FCSTD DOCUMENT  (FreeCAD 1.0R39285 (Git))
Label: full_assembly
License: All rights reserved
LicenseURL: http://en.wikipedia.org/wiki/All_rights_reserved
objects: App::Link×6, App::FeaturePython×6, Assembly::JointGroup×1, Assembly::AssemblyObject×1
EXTERNAL_REF file=front_plate.FCStd obj=Body
EXTERNAL_REF file=bottom_plate.FCStd obj=Body
EXTERNAL_REF file=side_left.FCStd obj=Clone
EXTERNAL_REF file=side_right.FCStd obj=Body
EXTERNAL_REF file=button.FCStd obj=Body
EXTERNAL_REF file=obd_wire_top.FCStd obj=Body

FEATURE [App::Link] Body
  LinkedObject = -> <external front_plate.FCStd>#Body
FEATURE [App::FeaturePython] GroundedJoint  # Assembly grounded joint (typed FeaturePython)
  ObjectToGround = -> Body
FEATURE [App::Link] Body001
  LinkPlacement = pos=(-1.29e-14,-21.3868,-88.9) rot=(1,0,0;4.71239rad)
  LinkedObject = -> <external bottom_plate.FCStd>#Body
  Placement = pos=(-1.29e-14,-21.3868,-88.9) rot=(1,0,0;4.71239rad)
FEATURE [App::Link] Hole001
  LinkPlacement = pos=(-84.328,1e-16,-76.2) rot=(0,-1,0;1.5708rad)
  LinkedObject = -> <external side_left.FCStd>#Clone
  Placement = pos=(-84.328,1e-16,-76.2) rot=(0,-1,0;1.5708rad)
FEATURE [App::Link] Body002
  LinkPlacement = pos=(84.328,-1.07e-14,-76.2) rot=(0,1,0;4.71239rad)
  LinkedObject = -> <external side_right.FCStd>#Body
  Placement = pos=(84.328,-1.07e-14,-76.2) rot=(0,1,0;4.71239rad)
FEATURE [App::FeaturePython] Joint  label="Fixed"  # Assembly joint (typed FeaturePython)
  Activated = true
  AngleMax = 0
  AngleMin = 0
  Detach1 = false
  Detach2 = false
  Distance = 0
  Distance2 = 0
  EnableAngleMax = false
  EnableAngleMin = false
  EnableLengthMax = false
  EnableLengthMin = false
  JointType = 0 (Fixed)
  LengthMax = 0
  LengthMin = 0
  Placement1 = pos=(-84.328,12.7,-19.05) rot=(0.707107,0,0.707107;3.14159rad)
  Placement2 = pos=(57.15,12.7,0) rot=(0,0,1;0rad)
  Reference1 = -> Assembly [Body.Edge87,Body.Edge87]
  Reference2 = -> Assembly [Hole001.Edge12,Hole001.Edge12]
FEATURE [App::FeaturePython] Joint002  label="Fixed002"  # Assembly joint (typed FeaturePython)
  Activated = true
  AngleMax = 0
  AngleMin = 0
  Detach1 = false
  Detach2 = false
  Distance = 0
  Distance2 = 0
  EnableAngleMax = false
  EnableAngleMin = false
  EnableLengthMax = false
  EnableLengthMin = false
  JointType = 0 (Fixed)
  LengthMax = 0
  LengthMin = 0
  Offset2 = pos=(0,0,0) rot=(0,0,-1;1.5708rad)
  Placement1 = pos=(74.168,-45.72,0) rot=(0,0,1;0rad)
  Placement2 = pos=(33.02,-21.3868,10.16) rot=(0.57735,-0.57735,-0.57735;4.18879rad)
  Reference1 = -> Assembly [Body001.?Edge13,Body001.?Edge13]
  Reference2 = -> Assembly [Body002.Edge68,Body002.Edge68]
FEATURE [App::Link] Body003
  LinkPlacement = pos=(43.2139,20.4026,-0.30034) rot=(0,0,1;0rad)
  LinkedObject = -> <external button.FCStd>#Body
  Placement = pos=(43.2139,20.4026,-0.30034) rot=(0,0,1;0rad)
FEATURE [App::FeaturePython] Joint003  label="Slider"  # Assembly joint (typed FeaturePython)
  Activated = true
  AngleMax = 0
  AngleMin = 0
  Detach1 = false
  Detach2 = false
  Distance = 0
  Distance2 = 0
  EnableAngleMax = false
  EnableAngleMin = false
  EnableLengthMax = false
  EnableLengthMin = false
  JointType = 3 (Slider)
  LengthMax = 0
  LengthMin = 0
  Placement1 = pos=(43.2139,20.4026,4.0132) rot=(0,0,1;0rad)
  Placement2 = pos=(0,0,5.08) rot=(0,0,1;0rad)
  Reference1 = -> Assembly [Body.Edge71,Body.Edge71]
  Reference2 = -> Assembly [Body003.Face4,Body003.Face4]
FEATURE [App::FeaturePython] Joint004  label="Fixed003"  # Assembly joint (typed FeaturePython)
  Activated = true
  AngleMax = 0
  AngleMin = 0
  Detach1 = false
  Detach2 = false
  Distance = 0
  Distance2 = 0
  EnableAngleMax = false
  EnableAngleMin = false
  EnableLengthMax = false
  EnableLengthMin = false
  JointType = 0 (Fixed)
  LengthMax = 0
  LengthMin = 0
  Placement1 = pos=(84.328,12.7,-19.05) rot=(0,-1,0;1.5708rad)
  Placement2 = pos=(57.15,12.7,0) rot=(0,0,1;0rad)
  Reference1 = -> Assembly [Body.Face48,Body.Edge1]
  Reference2 = -> Assembly [Body002.Face13,Body002.Edge3]
FEATURE [App::Link] Body004
  LinkPlacement = pos=(3.77944,9.05724,-256.163) rot=(0.57735,0.57735,-0.57735;2.0944rad)
  LinkedObject = -> <external obd_wire_top.FCStd>#Body
  Placement = pos=(3.77944,9.05724,-256.163) rot=(0.57735,0.57735,-0.57735;2.0944rad)
FEATURE [App::FeaturePython] GroundedJoint001  # Assembly grounded joint (typed FeaturePython)
  ObjectToGround = -> Body001
  Placement = pos=(-1.29e-14,-21.3868,-88.9) rot=(1,0,0;4.71239rad)
FEATURE [Assembly::JointGroup] Joints
  Group = -> [GroundedJoint,Joint,Joint002,Joint003,Joint004,GroundedJoint001]
FEATURE [Assembly::AssemblyObject] Assembly
  Group = -> [Joints,Body,GroundedJoint,Body001,Hole001,Body002,Joint,Joint002,Body003,Joint003,Joint004,GroundedJoint001,Body004]
  Origin = -> Origin
  Type = Assembly

RESOLVED EXTERNAL PARTS (link-assembly join: the EXTERNAL_REF files above that resolve inside this repo's crawl, each included once):
---- part bottom_plate.FCStd = doc fcstd_007f6532ab22 ----
FCSTD DOCUMENT  (FreeCAD 1.0R39285 (Git))
Label: bottom_plate
License: All rights reserved
LicenseURL: http://en.wikipedia.org/wiki/All_rights_reserved
objects: PartDesign::Pad×7, Sketcher::SketchObject×5, PartDesign::Plane×4, PartDesign::Pocket×1, PartDesign::Fillet×1, PartDesign::Body×1, Measure::MeasureLength×1
note: 42 computed .brp shape members not serialized (recipe doc carries the construction recipe); baked Part::Feature solids carry a one-line shape summary decoded from their .brp

FEATURE [Sketcher::SketchObject] Sketch
  ArcFitTolerance = 1e-06
  AttachmentSupport = -> [XY_Plane]
  FullyConstrained = true
  MakeInternals = false
  MapMode = 5
  sketch-geometry (13):
    g0: LineSegment StartX=-79.248 StartY=50.8 StartZ=0 EndX=-79.248 EndY=-50.8 EndZ=0
    g1: LineSegment StartX=-79.248 StartY=-50.8 StartZ=0 EndX=79.248 EndY=-50.8 EndZ=0
    g2: LineSegment StartX=79.248 StartY=-50.8 StartZ=0 EndX=79.248 EndY=50.8 EndZ=0
    g3: LineSegment StartX=79.248 StartY=50.8 StartZ=0 EndX=-79.248 EndY=50.8 EndZ=0
    g4: GeomPoint [constr] X=0 Y=0 Z=0
    g5: LineSegment [constr] StartX=-79.248 StartY=50.8 StartZ=0 EndX=-74.168 EndY=45.72 EndZ=0
    g6: LineSegment [constr] StartX=-79.248 StartY=-50.8 StartZ=0 EndX=-74.168 EndY=-45.72 EndZ=0
    g7: LineSegment [constr] StartX=79.248 StartY=-50.8 StartZ=0 EndX=74.168 EndY=-45.72 EndZ=0
    g8: LineSegment [constr] StartX=79.248 StartY=50.8 StartZ=0 EndX=74.168 EndY=45.72 EndZ=0
    g9: Circle CenterX=-74.168 CenterY=45.72 CenterZ=0 NormalX=0 NormalY=0 NormalZ=1 AngleXU=0 Radius=1.5875
    g10: Circle CenterX=-74.168 CenterY=-45.72 CenterZ=0 NormalX=0 NormalY=0 NormalZ=1 AngleXU=0 Radius=1.5875
    g11: Circle CenterX=74.168 CenterY=-45.72 CenterZ=0 NormalX=0 NormalY=0 NormalZ=1 AngleXU=0 Radius=1.5875
    g12: Circle CenterX=74.168 CenterY=45.72 CenterZ=0 NormalX=0 NormalY=0 NormalZ=1 AngleXU=0 Radius=1.5875
  constraints (32):
    c: Coincident(g0,g1)
    c: Coincident(g1,g2)
    c: Coincident(g2,g3)
    c: Coincident(g3,g0)
    c: Vertical(g0)
    c: Vertical(g2)
    c: Horizontal(g1)
    c: Horizontal(g3)
    c: Symmetric(g2,g0,g4)
    c: Distance(g0,g2) = 158.496
    c: Coincident(g4,g-1)
    c: Distance(g0,g0) = 101.6
    c: DistanceX(g5,g5) = 5.08
    c: DistanceY(g5,g5) = 5.08
    c: Coincident(g5,g0)
    c: DistanceX(g6,g6) = 5.08
    c: DistanceY(g6,g6) = 5.08
    c: Coincident(g6,g0)
    c: DistanceX(g7,g7) = 5.08
    c: DistanceY(g7,g7) = 5.08
    c: Coincident(g7,g1)
    c: DistanceX(g8,g8) = 5.08
    c: DistanceY(g8,g8) = 5.08
    c: Coincident(g8,g2)
    c: Diameter(g9) = 3.175
    c: Coincident(g9,g5)
    c: Diameter(g10) = 3.175
    c: Coincident(g10,g6)
    c: Diameter(g11) = 3.175
    c: Coincident(g11,g7)
    c: Diameter(g12) = 3.175
    c: Coincident(g12,g8)
FEATURE [PartDesign::Pad] Pad
  Direction = (0,0,1)
  Length = 4.0132
  Length2 = 10
  Profile = -> Sketch
  ReferenceAxis = -> Sketch [N_Axis]
  Suppressed = false
  Type = 0
FEATURE [PartDesign::Pad] Pad001
  BaseFeature = -> Pad
  Direction = (0,-1,0)
  Length = 25.4
  Length2 = 10
  Profile = -> Pad [Face2]
  Refine = true
  Suppressed = false
  Type = 0
FEATURE [PartDesign::Plane] DatumPlane
  AttachmentSupport = -> [Pad001]
  Length = 186.871
  MapMode = 5
  Placement = pos=(0,0,4.0132) rot=(0,0,1;0rad)
  ResizeMode = 0
  Width = 155.375
FEATURE [Sketcher::SketchObject] Sketch001
  ArcFitTolerance = 1e-06
  AttachmentSupport = -> [Pad001]
  ExternalGeometry = -> [Pad001]
  FullyConstrained = false
  MakeInternals = false
  MapMode = 5
  Placement = pos=(0,0,4.0132) rot=(0,0,1;0rad)
  sketch-geometry (59):
    g0: LineSegment [constr] StartX=14.4313 StartY=-24.9319 StartZ=0 EndX=14.4313 EndY=-63.0319 EndZ=0
    g1: LineSegment [constr] StartX=14.4313 StartY=-63.0319 StartZ=0 EndX=65.2313 EndY=-63.0319 EndZ=0
    g2: LineSegment [constr] StartX=65.2313 StartY=-63.0319 StartZ=0 EndX=65.2313 EndY=-24.9319 EndZ=0
    g3: LineSegment [constr] StartX=65.2313 StartY=-24.9319 StartZ=0 EndX=14.4313 EndY=-24.9319 EndZ=0
    g4: LineSegment [constr] StartX=-65.2313 StartY=-24.9319 StartZ=0 EndX=-65.2313 EndY=-63.0319 EndZ=0
    g5: LineSegment [constr] StartX=-65.2313 StartY=-63.0319 StartZ=0 EndX=-14.4313 EndY=-63.0319 EndZ=0
    g6: LineSegment [constr] StartX=-14.4313 StartY=-63.0319 StartZ=0 EndX=-14.4313 EndY=-24.9319 EndZ=0
    g7: LineSegment [constr] StartX=-14.4313 StartY=-24.9319 StartZ=0 EndX=-65.2313 EndY=-24.9319 EndZ=0
    g8: LineSegment [constr] StartX=-14.4313 StartY=-63.0319 StartZ=0 EndX=14.4313 EndY=-63.0319 EndZ=0
    g9: LineSegment [constr] StartX=-65.2313 StartY=43.3911 StartZ=0 EndX=-65.2313 EndY=-8.67892 EndZ=0
    g10: LineSegment [constr] StartX=-65.2313 StartY=-8.67892 StartZ=0 EndX=23.6687 EndY=-8.67892 EndZ=0
    g11: LineSegment [constr] StartX=23.6687 StartY=-8.67892 StartZ=0 EndX=23.6687 EndY=43.3911 EndZ=0
    g12: LineSegment [constr] StartX=23.6687 StartY=43.3911 StartZ=0 EndX=-65.2313 EndY=43.3911 EndZ=0
    g13: LineSegment [constr] StartX=45.5463 StartY=-8.67892 StartZ=0 EndX=65.2313 EndY=-8.67892 EndZ=0
    g14: LineSegment [constr] StartX=65.2313 StartY=-8.67892 StartZ=0 EndX=65.2313 EndY=37.4221 EndZ=0
    g15: LineSegment [constr] StartX=65.2313 StartY=37.4221 StartZ=0 EndX=45.5463 EndY=37.4221 EndZ=0
    g16: LineSegment [constr] StartX=45.5463 StartY=37.4221 StartZ=0 EndX=45.5463 EndY=-8.67892 EndZ=0
    g17: LineSegment [constr] StartX=-65.2313 StartY=-63.0319 StartZ=0 EndX=-79.248 EndY=-63.0319 EndZ=0
    g18: LineSegment [constr] StartX=65.2313 StartY=-63.0319 StartZ=0 EndX=79.248 EndY=-63.0319 EndZ=0
    g19: LineSegment [constr] StartX=-65.2313 StartY=-8.67892 StartZ=0 EndX=65.2313 EndY=-8.67892 EndZ=0
    g20: LineSegment [constr] StartX=19.5748 StartY=-43.9819 StartZ=0 EndX=60.0878 EndY=-43.9819 EndZ=0
    g21: LineSegment [constr] StartX=60.0878 StartY=-43.9819 StartZ=0 EndX=60.0878 EndY=-63.0319 EndZ=0
    g22: LineSegment [constr] StartX=60.0878 StartY=-43.9819 StartZ=0 EndX=60.0878 EndY=-24.9319 EndZ=0
    g23: LineSegment [constr] StartX=60.0878 StartY=-43.9819 StartZ=0 EndX=65.2313 EndY=-43.9819 EndZ=0
    g24: LineSegment [constr] StartX=19.5748 StartY=-43.9819 StartZ=0 EndX=14.4313 EndY=-43.9819 EndZ=0
    g25: LineSegment [constr] StartX=-65.2313 StartY=-43.9819 StartZ=0 EndX=-60.0878 EndY=-43.9819 EndZ=0
    g26: LineSegment [constr] StartX=-14.4313 StartY=-43.9819 StartZ=0 EndX=-19.5748 EndY=-43.9819 EndZ=0
    g27: LineSegment [constr] StartX=-60.0878 StartY=-43.9819 StartZ=0 EndX=-19.5748 EndY=-43.9819 EndZ=0
    g28: LineSegment [constr] StartX=-65.2313 StartY=17.3561 StartZ=0 EndX=-57.6113 EndY=17.3561 EndZ=0
    g29: LineSegment [constr] StartX=23.6687 StartY=17.3561 StartZ=0 EndX=16.0487 EndY=17.3561 EndZ=0
    g30: LineSegment [constr] StartX=-57.6113 StartY=17.3561 StartZ=0 EndX=16.0487 EndY=17.3561 EndZ=0
    g31: LineSegment [constr] StartX=55.3888 StartY=-8.67892 StartZ=0 EndX=55.3888 EndY=7.06908 EndZ=0
    g32: LineSegment [constr] StartX=55.3888 StartY=37.4221 StartZ=0 EndX=55.3888 EndY=21.6741 EndZ=0
    g33: LineSegment [constr] StartX=55.3888 StartY=7.06908 StartZ=0 EndX=55.3888 EndY=21.6741 EndZ=0
    g34: Circle CenterX=-60.0878 CenterY=-43.9819 CenterZ=0 NormalX=0 NormalY=0 NormalZ=1 AngleXU=0 Radius=2.54
    g35: Circle CenterX=-19.5748 CenterY=-43.9819 CenterZ=0 NormalX=0 NormalY=0 NormalZ=1 AngleXU=0 Radius=2.54
    g36: Circle CenterX=19.5748 CenterY=-43.9819 CenterZ=0 NormalX=0 NormalY=0 NormalZ=1 AngleXU=0 Radius=2.54
    g37: Circle CenterX=60.0878 CenterY=-43.9819 CenterZ=0 NormalX=0 NormalY=0 NormalZ=1 AngleXU=0 Radius=2.54
    g38: Circle CenterX=16.0487 CenterY=17.3561 CenterZ=0 NormalX=0 NormalY=0 NormalZ=1 AngleXU=0 Radius=2.54
    g39: Circle CenterX=55.3888 CenterY=7.06908 CenterZ=0 NormalX=0 NormalY=0 NormalZ=1 AngleXU=0 Radius=2.54
    g40: Circle CenterX=55.3888 CenterY=21.6741 CenterZ=0 NormalX=0 NormalY=0 NormalZ=1 AngleXU=0 Radius=2.54
    g41: Circle CenterX=-57.6113 CenterY=17.3561 CenterZ=0 NormalX=0 NormalY=0 NormalZ=1 AngleXU=0 Radius=2.54
    g42: LineSegment [constr] StartX=65.2313 StartY=-24.9319 StartZ=0 EndX=65.2313 EndY=-8.67892 EndZ=0
    g43: LineSegment [constr] StartX=-65.2313 StartY=-8.67892 StartZ=0 EndX=-65.2313 EndY=-24.9319 EndZ=0
    g44: Circle CenterX=-57.6113 CenterY=17.3561 CenterZ=0 NormalX=0 NormalY=0 NormalZ=1 AngleXU=0 Radius=0.992188
    g45: Circle CenterX=-19.5748 CenterY=-43.9819 CenterZ=0 NormalX=0 NormalY=0 NormalZ=1 AngleXU=0 Radius=0.992188
    g46: Circle CenterX=19.5748 CenterY=-43.9819 CenterZ=0 NormalX=0 NormalY=0 NormalZ=1 AngleXU=0 Radius=0.992188
    g47: Circle CenterX=55.3888 CenterY=7.06908 CenterZ=0 NormalX=0 NormalY=0 NormalZ=1 AngleXU=0 Radius=0.992188
    g48: Circle CenterX=55.3888 CenterY=21.6741 CenterZ=0 NormalX=0 NormalY=0 NormalZ=1 AngleXU=0 Radius=0.992188
    g49: LineSegment [constr] StartX=-65.2313 StartY=-16.8054 StartZ=0 EndX=-79.248 EndY=-16.8054 EndZ=0
    g50: LineSegment StartX=-74.1447 StartY=-24.1079 StartZ=0 EndX=-70.3347 EndY=-24.1079 EndZ=0
    g51: LineSegment StartX=-70.3347 StartY=-24.1079 StartZ=0 EndX=-70.3347 EndY=-9.5029 EndZ=0
    g52: LineSegment StartX=-70.3347 StartY=-9.5029 StartZ=0 EndX=-74.1447 EndY=-9.5029 EndZ=0
    g53: LineSegment StartX=-74.1447 StartY=-9.5029 StartZ=0 EndX=-74.1447 EndY=-24.1079 EndZ=0
    g54: GeomPoint [constr] X=-72.2397 Y=-16.8054 Z=0
    g55: LineSegment [constr] StartX=-72.2397 StartY=-24.1079 StartZ=0 EndX=-72.2397 EndY=-22.2029 EndZ=0
    g56: LineSegment [constr] StartX=-72.2397 StartY=-9.5029 StartZ=0 EndX=-72.2397 EndY=-11.4079 EndZ=0
    g57: Circle CenterX=-72.2397 CenterY=-11.4079 CenterZ=0 NormalX=0 NormalY=0 NormalZ=1 AngleXU=0 Radius=0.992188
    g58: Circle CenterX=-72.2397 CenterY=-22.2029 CenterZ=0 NormalX=0 NormalY=0 NormalZ=1 AngleXU=0 Radius=0.992188
  constraints (148):
    c: Coincident(g0,g1)
    c: Coincident(g1,g2)
    c: Coincident(g2,g3)
    c: Coincident(g3,g0)
    c: Vertical(g0)
    c: Vertical(g2)
    c: Horizontal(g1)
    c: Horizontal(g3)
    c: Coincident(g4,g5)
    c: Coincident(g5,g6)
    c: Coincident(g6,g7)
    c: Coincident(g7,g4)
    c: Vertical(g4)
    c: Vertical(g6)
    c: Horizontal(g5)
    c: Horizontal(g7)
    c: Distance(g4,g6) = 50.8
    c: Distance(g5,g7) = 38.1
    c: Coincident(g8,g5)
    c: Coincident(g8,g0)
    c: Horizontal(g8)
    c: Coincident(g9,g10)
    c: Coincident(g10,g11)
    c: Coincident(g11,g12)
    c: Coincident(g12,g9)
    c: Vertical(g9)
    c: Vertical(g11)
    c: Horizontal(g10)
    c: Horizontal(g12)
    c: Distance(g9,g11) = 88.9
    c: Distance(g10,g12) = 52.07
    c: Coincident(g13,g14)
    c: Coincident(g14,g15)
    c: Coincident(g15,g16)
    c: Coincident(g16,g13)
    c: Horizontal(g13)
    c: Horizontal(g15)
    c: Vertical(g14)
    c: Vertical(g16)
    c: Distance(g14,g16) = 19.685
    c: Distance(g13,g15) = 46.101
    c: Coincident(g17,g4)
    c: PointOnObject(g17,g-4)
    c: Horizontal(g17)
    c: Coincident(g18,g1)
    c: PointOnObject(g18,g-6)
    c: Horizontal(g18)
    c: Equal(g18,g17)
    c: Coincident(g19,g9)
    c: Coincident(g19,g13)
    c: Horizontal(g19)
    c: Distance(g20) = 40.513
    c: Horizontal(g20)
    c: Coincident(g21,g20)
    c: PointOnObject(g21,g1)
    c: Vertical(g21)
    c: Coincident(g22,g20)
    c: PointOnObject(g22,g3)
    c: Vertical(g22)
    c: Coincident(g23,g20)
    c: Symmetric(g2,g2,g23)
    c: Coincident(g24,g20)
    c: Symmetric(g0,g0,g24)
    c: Equal(g22,g21)
    c: Equal(g23,g24)
    c: Symmetric(g4,g4,g25)
    c: Horizontal(g25)
    c: Symmetric(g6,g6,g26)
    c: Horizontal(g26)
    c: Coincident(g27,g25)
    c: Coincident(g27,g26)
    c: DistanceX(g27,g27) = 40.513
    c: Equal(g26,g25)
    c: Symmetric(g9,g9,g28)
    c: Horizontal(g28)
    c: Symmetric(g11,g11,g29)
    c: Horizontal(g29)
    c: Coincident(g30,g28)
    c: Coincident(g30,g29)
    c: DistanceX(g30,g30) = 73.66
    c: Equal(g29,g28)
    c: Symmetric(g13,g13,g31)
    c: Vertical(g31)
    c: Symmetric(g15,g15,g32)
    c: Vertical(g32)
    c: Coincident(g33,g31)
    c: Coincident(g33,g32)
    c: DistanceY(g33,g33) = 14.605
    c: Equal(g32,g31)
    c: Diameter(g34) = 5.08
    c: Coincident(g34,g25)
    c: Diameter(g35) = 5.08
    c: Coincident(g35,g26)
    c: Diameter(g36) = 5.08
    c: Coincident(g36,g20)
    c: Diameter(g37) = 5.08
    c: Coincident(g37,g20)
    c: Diameter(g38) = 5.08
    c: Coincident(g38,g29)
    c: Diameter(g39) = 5.08
    c: Coincident(g39,g31)
    c: Diameter(g40) = 5.08
    c: Coincident(g40,g32)
    c: Equal(g7,g3)
    c: Equal(g4,g0)
    c: Diameter(g41) = 5.08
    c: Coincident(g41,g28)
    c: Coincident(g42,g2)
    c: Coincident(g42,g13)
    c: Coincident(g43,g9)
    c: Coincident(g43,g4)
    c: Vertical(g43)
    c: Vertical(g42)
    c: Diameter(g44) = 1.98438
    c: Coincident(g44,g28)
    c: Coincident(g45,g26)
    c: Coincident(g46,g20)
    c: Coincident(g47,g31)
    c: Coincident(g48,g32)
    c: Equal(g44,g45)
    c: Equal(g46,g44)
    c: Equal(g44,g47)
    c: Equal(g47,g48)
    c: Symmetric(g43,g43,g49)
    c: PointOnObject(g49,g-4)
    c: Horizontal(g49)
    c: Coincident(g50,g51)
    c: Coincident(g51,g52)
    c: Coincident(g52,g53)
    c: Coincident(g53,g50)
    c: Horizontal(g50)
    c: Horizontal(g52)
    c: Vertical(g51)
    c: Vertical(g53)
    c: Symmetric(g52,g50,g54)
    c: Distance(g51,g53) = 3.81
    c: Distance(g50,g52) = 14.605
    c: Symmetric(g49,g49,g54)
    c: Distance(g55) = 1.905
    c: Symmetric(g50,g50,g55)
    c: Vertical(g55)
    c: Distance(g56) = 1.905
    c: Symmetric(g52,g52,g56)
    c: Vertical(g56)
    c: Diameter(g57) = 1.98438
    c: Coincident(g57,g56)
    c: Coincident(g58,g55)
    c: Equal(g57,g58)
FEATURE [PartDesign::Pad] Pad002
  BaseFeature = -> Pad001
  Direction = (0,0,1)
  Length = 7.62
  Length2 = 10
  Profile = -> Sketch001
  ReferenceAxis = -> Sketch001 [N_Axis]
  Refine = true
  Suppressed = false
  Type = 0
FEATURE [PartDesign::Pad] Pad003
  BaseFeature = -> Pad002
  Direction = (0,0,1)
  Length = 0.254
  Length2 = 10
  Profile = -> Pad002 [Face23,Face27]
  Refine = true
  Suppressed = false
  Type = 0
FEATURE [PartDesign::Pad] Pad004
  BaseFeature = -> Pad003
  Direction = (0,0,1)
  Length = 0.508
  Length2 = 10
  Profile = -> Pad003 [Face25]
  Refine = true
  Suppressed = false
  Type = 0
FEATURE [PartDesign::Plane] DatumPlane001
  AttachmentSupport = -> [Pad004]
  Length = 186.871
  MapMode = 5
  Placement = pos=(0,0,11.8872) rot=(0,0,1;0rad)
  ResizeMode = 0
  Width = 155.375
FEATURE [Sketcher::SketchObject] Sketch002
  ArcFitTolerance = 1e-06
  AttachmentSupport = -> [Pad004]
  ExternalGeometry = -> [Pad004]
  FullyConstrained = true
  MakeInternals = false
  MapMode = 5
  Placement = pos=(0,0,11.8872) rot=(0,0,1;0rad)
  sketch-geometry (2):
    g0: Circle CenterX=60.0878 CenterY=-43.9819 CenterZ=0 NormalX=0 NormalY=0 NormalZ=1 AngleXU=0 Radius=1.4605
    g1: Circle CenterX=-60.0878 CenterY=-43.9819 CenterZ=0 NormalX=0 NormalY=0 NormalZ=1 AngleXU=0 Radius=1.4605
  constraints (4):
    c: Diameter(g0) = 2.921
    c: Coincident(g0,g-4)
    c: Diameter(g1) = 2.921
    c: Coincident(g1,g-3)
FEATURE [PartDesign::Pad] Pad005
  BaseFeature = -> Pad004
  Direction = (0,0,1)
  Length = 1.524
  Length2 = 10
  Profile = -> Sketch002
  ReferenceAxis = -> Sketch002 [N_Axis]
  Refine = true
  Suppressed = false
  Type = 0
FEATURE [PartDesign::Plane] DatumPlane002
  AttachmentSupport = -> [Pad005]
  Length = 155.375
  MapMode = 11
  Placement = pos=(16.0487,17.3561,12.1412) rot=(0,0,1;1.5708rad)
  ResizeMode = 0
  Width = 186.871
FEATURE [Sketcher::SketchObject] Sketch003
  ArcFitTolerance = 1e-06
  AttachmentSupport = -> [DatumPlane002]
  ExternalGeometry = -> [Pad005]
  FullyConstrained = true
  MakeInternals = false
  MapMode = 5
  Placement = pos=(16.0487,17.3561,12.1412) rot=(0,0,1;1.5708rad)
  sketch-geometry (1):
    g0: Circle CenterX=0 CenterY=0 CenterZ=0 NormalX=0 NormalY=0 NormalZ=1 AngleXU=0 Radius=1.4605
  constraints (2):
    c: Diameter(g0) = 2.921
    c: Coincident(g0,g-1)
FEATURE [PartDesign::Pad] Pad006
  BaseFeature = -> Pad005
  Direction = (0,0,1)
  Length = 1.524
  Length2 = 10
  Profile = -> Sketch003
  ReferenceAxis = -> Sketch003 [N_Axis]
  Refine = true
  Suppressed = false
  Type = 0
FEATURE [PartDesign::Plane] DatumPlane003
  AttachmentSupport = -> [Pad003]
  Length = 142.937
  MapMode = 5
  Placement = pos=(-74.1447,0,0) rot=(0.57735,-0.57735,-0.57735;2.0944rad)
  ResizeMode = 0
  Width = 65.9374
FEATURE [Sketcher::SketchObject] Sketch004
  ArcFitTolerance = 1e-06
  AttachmentSupport = -> [Pad003]
  ExternalGeometry = -> [Pad003]
  FullyConstrained = true
  MakeInternals = false
  MapMode = 5
  Placement = pos=(-74.1447,0,0) rot=(0.57735,-0.57735,-0.57735;2.0944rad)
  sketch-geometry (1):
    g0: Circle CenterX=16.8054 CenterY=11.6332 CenterZ=0 NormalX=0 NormalY=0 NormalZ=1 AngleXU=0 Radius=3.4925
  constraints (2):
    c: Diameter(g0) = 6.985
    c: Symmetric(g-3,g-3,g0)
FEATURE [PartDesign::Pocket] Pocket
  BaseFeature = -> Pad006
  Direction = (1,0,0)
  Length = 5
  Length2 = 5
  Profile = -> Sketch004
  ReferenceAxis = -> Sketch004 [N_Axis]
  Refine = true
  Suppressed = false
  Type = 1
FEATURE [PartDesign::Fillet] Fillet
  Base = -> Pocket [Edge18,Edge19,Edge29,Edge27,Edge24,Edge31,Edge30,Edge25]
  BaseFeature = -> Pocket
  Radius = 3.175
  Refine = true
  SupportTransform = false
  Suppressed = false
  UseAllEdges = false
FEATURE [PartDesign::Body] Body
  AllowCompound = false
  Group = -> [Sketch,Pad,Pad001,DatumPlane,Sketch001,Pad002,Pad003,Pad004,DatumPlane001,Sketch002,Pad005,DatumPlane002,Sketch003,Pad006,DatumPlane003,Sketch004,Pocket,Fillet]
  Origin = -> Origin
  Tip = -> Fillet
FEATURE [Measure::MeasureLength] Length  label="Length: 0.1580 ""
  Elements = -> [Body]
  Length = 4.0132
---- part button.FCStd = doc fcstd_32a29ad11dd7 ----
FCSTD DOCUMENT  (FreeCAD 1.0R39285 (Git))
Label: button
License: All rights reserved
LicenseURL: http://en.wikipedia.org/wiki/All_rights_reserved
objects: PartDesign::Pad×3, Sketcher::SketchObject×2, PartDesign::Pocket×2, PartDesign::Fillet×1, PartDesign::Body×1
note: 23 computed .brp shape members not serialized (recipe doc carries the construction recipe); baked Part::Feature solids carry a one-line shape summary decoded from their .brp

FEATURE [Sketcher::SketchObject] Sketch
  ArcFitTolerance = 1e-06
  AttachmentSupport = -> [XY_Plane]
  FullyConstrained = true
  MakeInternals = false
  MapMode = 5
  sketch-geometry (10):
    g0: LineSegment StartX=-1.6129 StartY=-1.1049 StartZ=0 EndX=1.6129 EndY=-1.1049 EndZ=0
    g1: LineSegment StartX=1.6129 StartY=-1.1049 StartZ=0 EndX=1.6129 EndY=1.1049 EndZ=0
    g2: LineSegment StartX=1.6129 StartY=1.1049 StartZ=0 EndX=-1.6129 EndY=1.1049 EndZ=0
    g3: LineSegment StartX=-1.6129 StartY=1.1049 StartZ=0 EndX=-1.6129 EndY=-1.1049 EndZ=0
    g4: GeomPoint [constr] X=0 Y=0 Z=0
    g5: LineSegment StartX=-1.905 StartY=-1.905 StartZ=0 EndX=1.905 EndY=-1.905 EndZ=0
    g6: LineSegment StartX=1.905 StartY=-1.905 StartZ=0 EndX=1.905 EndY=1.905 EndZ=0
    g7: LineSegment StartX=1.905 StartY=1.905 StartZ=0 EndX=-1.905 EndY=1.905 EndZ=0
    g8: LineSegment StartX=-1.905 StartY=1.905 StartZ=0 EndX=-1.905 EndY=-1.905 EndZ=0
    g9: GeomPoint [constr] X=0 Y=0 Z=0
  constraints (24):
    c: Coincident(g0,g1)
    c: Coincident(g1,g2)
    c: Coincident(g2,g3)
    c: Coincident(g3,g0)
    c: Horizontal(g0)
    c: Horizontal(g2)
    c: Vertical(g1)
    c: Vertical(g3)
    c: Symmetric(g2,g0,g4)
    c: Distance(g1,g3) = 3.2258
    c: Distance(g0,g2) = 2.2098
    c: Coincident(g4,g-1)
    c: Coincident(g5,g6)
    c: Coincident(g6,g7)
    c: Coincident(g7,g8)
    c: Coincident(g8,g5)
    c: Horizontal(g5)
    c: Horizontal(g7)
    c: Vertical(g6)
    c: Vertical(g8)
    c: Symmetric(g7,g5,g9)
    c: Distance(g6,g8) = 3.81
    c: Distance(g5,g7) = 3.81
    c: Coincident(g9,g4)
FEATURE [PartDesign::Pad] Pad
  Direction = (0,0,1)
  Length = 2.54
  Length2 = 10
  Profile = -> Sketch
  ReferenceAxis = -> Sketch [N_Axis]
  Suppressed = false
  Type = 0
FEATURE [Sketcher::SketchObject] Sketch001
  ArcFitTolerance = 1e-06
  AttachmentSupport = -> [Pad]
  FullyConstrained = true
  MakeInternals = false
  MapMode = 5
  Placement = pos=(0,0,2.54) rot=(0,0,1;0rad)
  sketch-geometry (1):
    g0: Circle CenterX=0 CenterY=0 CenterZ=0 NormalX=0 NormalY=0 NormalZ=1 AngleXU=0 Radius=4.7625
  constraints (2):
    c: Diameter(g0) = 9.525
    c: Coincident(g0,g-1)
FEATURE [PartDesign::Pad] Pad001
  BaseFeature = -> Pad
  Direction = (0,0,1)
  Length = 2.54
  Length2 = 10
  Profile = -> Sketch001
  ReferenceAxis = -> Sketch001 [N_Axis]
  Suppressed = false
  Type = 0
FEATURE [PartDesign::Fillet] Fillet
  Base = -> Pad001 [Edge27]
  BaseFeature = -> Pad001
  Radius = 0.254
  SupportTransform = false
  Suppressed = false
  UseAllEdges = false
FEATURE [PartDesign::Pocket] Pocket
  BaseFeature = -> Fillet
  Direction = (0,0,1)
  Length = 2.286
  Length2 = 5
  Profile = -> Fillet [Face14]
  Refine = true
  Suppressed = false
  Type = 0
FEATURE [PartDesign::Pocket] Pocket001
  BaseFeature = -> Pocket
  Direction = (0,0,1)
  Length = 2.286
  Length2 = 5
  Profile = -> Pocket [Face11]
  Refine = true
  Suppressed = false
  Type = 0
FEATURE [PartDesign::Pad] Pad002
  BaseFeature = -> Pocket001
  Direction = (0,0,-1)
  Length = 10
  Length2 = 10
  Profile = -> Pocket001 [Face11]
  Refine = true
  Suppressed = false
  Type = 3
  UpToFace = -> Pocket001 [Face6]
FEATURE [PartDesign::Body] Body
  AllowCompound = false
  Group = -> [Sketch,Pad,Sketch001,Pad001,Fillet,Pocket,Pocket001,Pad002]
  Origin = -> Origin
  Tip = -> Pad002
---- part front_plate.FCStd = doc fcstd_a2606d69e9d5 ----
FCSTD DOCUMENT  (FreeCAD 1.0R39285 (Git))
Label: front_plate
License: All rights reserved
LicenseURL: http://en.wikipedia.org/wiki/All_rights_reserved
objects: Sketcher::SketchObject×6, PartDesign::Pad×3, PartDesign::Hole×2, PartDesign::Pocket×1, PartDesign::Body×1
note: 31 computed .brp shape members not serialized (recipe doc carries the construction recipe); baked Part::Feature solids carry a one-line shape summary decoded from their .brp

FEATURE [Sketcher::SketchObject] Sketch
  ArcFitTolerance = 1e-06
  AttachmentSupport = -> [XY_Plane]
  FullyConstrained = false
  MakeInternals = false
  MapMode = 5
  sketch-geometry (46):
    g0: LineSegment StartX=-93.6625 StartY=-28.575 StartZ=0 EndX=93.6625 EndY=-28.575 EndZ=0
    g1: LineSegment StartX=93.6625 StartY=-28.575 StartZ=0 EndX=93.6625 EndY=28.575 EndZ=0
    g2: LineSegment StartX=93.6625 StartY=28.575 StartZ=0 EndX=-93.6625 EndY=28.575 EndZ=0
    g3: LineSegment StartX=-93.6625 StartY=28.575 StartZ=0 EndX=-93.6625 EndY=-28.575 EndZ=0
    g4: GeomPoint [constr] X=0 Y=0 Z=0
    g5: LineSegment [constr] StartX=-88.9 StartY=-25.4 StartZ=0 EndX=88.9 EndY=-25.4 EndZ=0
    g6: LineSegment [constr] StartX=88.9 StartY=-25.4 StartZ=0 EndX=88.9 EndY=25.4 EndZ=0
    g7: LineSegment [constr] StartX=88.9 StartY=25.4 StartZ=0 EndX=-88.9 EndY=25.4 EndZ=0
    g8: LineSegment [constr] StartX=-88.9 StartY=25.4 StartZ=0 EndX=-88.9 EndY=-25.4 EndZ=0
    g9: GeomPoint [constr] X=0 Y=0 Z=0
    g10: GeomPoint [constr] X=-66.9291 Y=0 Z=0
    g11: LineSegment StartX=79.0152 StartY=12.2301 StartZ=0 EndX=7.41257 EndY=12.2301 EndZ=0
    g12: LineSegment StartX=79.0152 StartY=-12.2301 StartZ=0 EndX=79.0152 EndY=12.2301 EndZ=0
    g13: LineSegment StartX=7.41257 StartY=-12.2301 StartZ=0 EndX=79.0152 EndY=-12.2301 EndZ=0
    g14: LineSegment StartX=7.41257 StartY=12.2301 StartZ=0 EndX=7.41257 EndY=-12.2301 EndZ=0
    g15: LineSegment [constr] StartX=79.0152 StartY=-12.2301 StartZ=0 EndX=93.6625 EndY=-12.2301 EndZ=0
    g16: LineSegment StartX=-7.23477 StartY=-12.2301 StartZ=0 EndX=-78.8374 EndY=-12.2301 EndZ=0
    g17: LineSegment StartX=-78.8374 StartY=-12.2301 StartZ=0 EndX=-78.8374 EndY=12.2301 EndZ=0
    g18: LineSegment StartX=-78.8374 StartY=12.2301 StartZ=0 EndX=-7.23477 EndY=12.2301 EndZ=0
    g19: LineSegment StartX=-7.23477 StartY=12.2301 StartZ=0 EndX=-7.23477 EndY=-12.2301 EndZ=0
    g20: LineSegment [constr] StartX=-78.8374 StartY=-12.2301 StartZ=0 EndX=-93.6625 EndY=-12.2301 EndZ=0
    g21: LineSegment [constr] StartX=-7.23477 StartY=-12.2301 StartZ=0 EndX=7.41257 EndY=-12.2301 EndZ=0
    g22: LineSegment [constr] StartX=-78.8374 StartY=12.2301 StartZ=0 EndX=-78.8374 EndY=28.575 EndZ=0
    g23: GeomPoint [constr] X=-78.8374 Y=20.4026 Z=0
    g24: LineSegment [constr] StartX=-78.8374 StartY=20.4026 StartZ=0 EndX=-77.3388 EndY=20.4026 EndZ=0
    g25: Circle CenterX=-77.3388 CenterY=20.4026 CenterZ=0 NormalX=0 NormalY=0 NormalZ=1 AngleXU=0 Radius=1.5875
    g26: Circle CenterX=-70.5163 CenterY=20.4026 CenterZ=0 NormalX=0 NormalY=0 NormalZ=1 AngleXU=0 Radius=1.5875
    g27: Circle CenterX=-63.6939 CenterY=20.4026 CenterZ=0 NormalX=0 NormalY=0 NormalZ=1 AngleXU=0 Radius=1.5875
    g28: Circle CenterX=-56.8714 CenterY=20.4026 CenterZ=0 NormalX=0 NormalY=0 NormalZ=1 AngleXU=0 Radius=1.5875
    g29: Circle CenterX=-50.049 CenterY=20.4026 CenterZ=0 NormalX=0 NormalY=0 NormalZ=1 AngleXU=0 Radius=1.5875
    g30: Circle CenterX=-43.2266 CenterY=20.4026 CenterZ=0 NormalX=0 NormalY=0 NormalZ=1 AngleXU=0 Radius=1.5875
    g31: Circle CenterX=-36.4041 CenterY=20.4026 CenterZ=0 NormalX=0 NormalY=0 NormalZ=1 AngleXU=0 Radius=1.5875
    g32: Circle CenterX=-29.5817 CenterY=20.4026 CenterZ=0 NormalX=0 NormalY=0 NormalZ=1 AngleXU=0 Radius=1.5875
    g33: Circle CenterX=-22.7592 CenterY=20.4026 CenterZ=0 NormalX=0 NormalY=0 NormalZ=1 AngleXU=0 Radius=1.5875
    g34: Circle CenterX=-15.9368 CenterY=20.4026 CenterZ=0 NormalX=0 NormalY=0 NormalZ=1 AngleXU=0 Radius=1.5875
    g35: Circle CenterX=-9.11437 CenterY=20.4026 CenterZ=0 NormalX=0 NormalY=0 NormalZ=1 AngleXU=0 Radius=1.5875
    g36: LineSegment [constr] StartX=-77.3388 StartY=20.4026 StartZ=0 EndX=-70.5163 EndY=20.4026 EndZ=0
    g37: LineSegment [constr] StartX=-70.5163 StartY=20.4026 StartZ=0 EndX=-63.6939 EndY=20.4026 EndZ=0
    g38: LineSegment [constr] StartX=-63.6939 StartY=20.4026 StartZ=0 EndX=-56.8714 EndY=20.4026 EndZ=0
    g39: LineSegment [constr] StartX=-56.8714 StartY=20.4026 StartZ=0 EndX=-50.049 EndY=20.4026 EndZ=0
    g40: LineSegment [constr] StartX=-50.049 StartY=20.4026 StartZ=0 EndX=-43.2266 EndY=20.4026 EndZ=0
    g41: LineSegment [constr] StartX=-43.2266 StartY=20.4026 StartZ=0 EndX=-36.4041 EndY=20.4026 EndZ=0
    g42: LineSegment [constr] StartX=-36.4041 StartY=20.4026 StartZ=0 EndX=-29.5817 EndY=20.4026 EndZ=0
    g43: LineSegment [constr] StartX=-29.5817 StartY=20.4026 StartZ=0 EndX=-22.7592 EndY=20.4026 EndZ=0
    g44: LineSegment [constr] StartX=-22.7592 StartY=20.4026 StartZ=0 EndX=-15.9368 EndY=20.4026 EndZ=0
    g45: LineSegment [constr] StartX=-15.9368 StartY=20.4026 StartZ=0 EndX=-9.11437 EndY=20.4026 EndZ=0
  constraints (110):
    c: Coincident(g0,g1)
    c: Coincident(g1,g2)
    c: Coincident(g2,g3)
    c: Coincident(g3,g0)
    c: Horizontal(g0)
    c: Horizontal(g2)
    c: Vertical(g1)
    c: Vertical(g3)
    c: Symmetric(g2,g0,g4)
    c: Distance(g1,g3) = 187.325
    c: Distance(g0,g2) = 57.15
    c: Coincident(g4,g-1)
    c: Coincident(g5,g6)
    c: Coincident(g6,g7)
    c: Coincident(g7,g8)
    c: Coincident(g8,g5)
    c: Horizontal(g5)
    c: Horizontal(g7)
    c: Vertical(g6)
    c: Vertical(g8)
    c: Symmetric(g7,g5,g9)
    c: Distance(g6,g8) = 177.8
    c: Distance(g5,g7) = 50.8
    c: Coincident(g9,g4)
    c: PointOnObject(g10,g-1)
    c: Coincident(g13,g12)
    c: Coincident(g12,g11)
    c: Coincident(g11,g14)
    c: Coincident(g14,g13)
    c: Horizontal(g13)
    c: Horizontal(g11)
    c: Vertical(g12)
    c: Vertical(g14)
    c: Distance(g12,g14) = 71.6026
    c: Distance(g13,g11) = 24.4602
    c: Coincident(g15,g12)
    c: PointOnObject(g15,g1)
    c: Horizontal(g15)
    c: Coincident(g16,g17)
    c: Coincident(g17,g18)
    c: Coincident(g18,g19)
    c: Coincident(g19,g16)
    c: Horizontal(g16)
    c: Horizontal(g18)
    c: Vertical(g17)
    c: Vertical(g19)
    c: Distance(g17,g19) = 71.6026
    c: Distance(g16,g18) = 24.4602
    c: Coincident(g20,g17)
    c: Horizontal(g20)
    c: Coincident(g21,g16)
    c: Coincident(g21,g13)
    c: Horizontal(g21)
    c: DistanceX(g21,g21) = 14.6473
    c: DistanceX(g15,g15) = 14.6473
    c: Coincident(g22,g17)
    c: PointOnObject(g22,g2)
    c: Vertical(g22)
    c: Symmetric(g22,g22,g23)
    c: Distance(g24) = 1.4986
    c: Horizontal(g24)
    c: Diameter(g25) = 3.175
    c: Diameter(g26) = 3.175
    c: Diameter(g27) = 3.175
    c: Diameter(g28) = 3.175
    c: Diameter(g29) = 3.175
    c: Diameter(g30) = 3.175
    c: Diameter(g31) = 3.175
    c: Diameter(g32) = 3.175
    c: Diameter(g33) = 3.175
    c: Diameter(g34) = 3.175
    c: Diameter(g35) = 3.175
    c: Distance(g16,g5) = 13.1699
    c: Distance(g25,g26) = 6.82244
    c: DistanceX(g26,g27) = 6.82244
    c: DistanceX(g27,g28) = 6.82244
    c: DistanceX(g28,g29) = 6.82244
    c: Distance(g29,g30) = 6.82244
    c: Distance(g30,g31) = 6.82244
    c: Distance(g31,g32) = 6.82244
    c: Distance(g32,g33) = 6.82244
    c: Distance(g33,g34) = 6.82244
    c: Distance(g34,g35) = 6.82244
    c: Coincident(g36,g25)
    c: Coincident(g36,g26)
    c: Horizontal(g36)
    c: Coincident(g37,g26)
    c: Coincident(g37,g27)
    c: Horizontal(g37)
    c: Coincident(g38,g27)
    c: Coincident(g38,g28)
    c: Horizontal(g38)
    c: Coincident(g39,g28)
    c: Coincident(g39,g29)
    c: Horizontal(g39)
    c: Coincident(g40,g29)
    c: Coincident(g40,g30)
    c: Horizontal(g40)
    c: Coincident(g41,g30)
    c: Coincident(g41,g31)
    c: Horizontal(g41)
    c: Coincident(g42,g31)
    c: Coincident(g42,g32)
    c: Horizontal(g42)
    c: Coincident(g43,g32)
    c: Coincident(g43,g33)
    c: Horizontal(g43)
    c: Coincident(g44,g33)
    c: Coincident(g44,g34)
    c: Horizontal(g44)
FEATURE [PartDesign::Pad] Pad
  Direction = (0,0,1)
  Length = 4.0132
  Length2 = 10
  Profile = -> Sketch
  ReferenceAxis = -> Sketch [N_Axis]
  Suppressed = false
  Type = 0
FEATURE [Sketcher::SketchObject] Sketch001
  ArcFitTolerance = 1e-06
  AttachmentSupport = -> [Pad]
  ExternalGeometry = -> [Pad]
  FullyConstrained = true
  MakeInternals = false
  MapMode = 5
  Placement = pos=(0,0,0) rot=(1,0,0;3.14159rad)
  sketch-geometry (26):
    g0: LineSegment [constr] StartX=79.0152 StartY=-12.2301 StartZ=0 EndX=80.6662 EndY=-16.1925 EndZ=0
    g1: LineSegment [constr] StartX=7.41257 StartY=-12.2301 StartZ=0 EndX=5.76157 EndY=-16.1925 EndZ=0
    g2: LineSegment [constr] StartX=79.0152 StartY=12.2301 StartZ=0 EndX=80.6662 EndY=15.1257 EndZ=0
    g3: LineSegment [constr] StartX=7.41257 StartY=12.2301 StartZ=0 EndX=5.76157 EndY=15.1257 EndZ=0
    g4: LineSegment [constr] StartX=-7.23477 StartY=12.2301 StartZ=0 EndX=-5.58377 EndY=15.1257 EndZ=0
    g5: LineSegment [constr] StartX=-78.8374 StartY=12.2301 StartZ=0 EndX=-80.4884 EndY=15.1257 EndZ=0
    g6: LineSegment [constr] StartX=-78.8374 StartY=-12.2301 StartZ=0 EndX=-80.4884 EndY=-16.1925 EndZ=0
    g7: LineSegment [constr] StartX=-7.23477 StartY=-12.2301 StartZ=0 EndX=-5.58377 EndY=-16.1925 EndZ=0
    g8: LineSegment [constr] StartX=5.76157 StartY=15.1257 StartZ=0 EndX=0 EndY=15.1257 EndZ=0
    g9: LineSegment StartX=-84.328 StartY=12.9032 StartZ=0 EndX=84.328 EndY=12.9032 EndZ=0
    g10: LineSegment StartX=84.328 StartY=12.9032 StartZ=0 EndX=84.328 EndY=17.3482 EndZ=0
    g11: LineSegment StartX=84.328 StartY=17.3482 StartZ=0 EndX=-84.328 EndY=17.3482 EndZ=0
    g12: LineSegment StartX=-84.328 StartY=17.3482 StartZ=0 EndX=-84.328 EndY=12.9032 EndZ=0
    g13: GeomPoint [constr] X=0 Y=15.1257 Z=0
    g14: Circle CenterX=80.6662 CenterY=-16.1925 CenterZ=0 NormalX=0 NormalY=0 NormalZ=1 AngleXU=0 Radius=2.54
    g15: Circle CenterX=5.76157 CenterY=-16.1925 CenterZ=0 NormalX=0 NormalY=0 NormalZ=1 AngleXU=0 Radius=2.54
    g16: Circle CenterX=-5.58377 CenterY=-16.1925 CenterZ=0 NormalX=0 NormalY=0 NormalZ=1 AngleXU=0 Radius=2.54
    g17: Circle CenterX=-80.4884 CenterY=-16.1925 CenterZ=0 NormalX=0 NormalY=0 NormalZ=1 AngleXU=0 Radius=2.54
    g18: Circle CenterX=80.6662 CenterY=-16.1925 CenterZ=0 NormalX=0 NormalY=0 NormalZ=1 AngleXU=0 Radius=1.016
    g19: Circle CenterX=5.76157 CenterY=-16.1925 CenterZ=0 NormalX=0 NormalY=0 NormalZ=1 AngleXU=0 Radius=1.016
    g20: Circle CenterX=-5.58377 CenterY=-16.1925 CenterZ=0 NormalX=0 NormalY=0 NormalZ=1 AngleXU=0 Radius=1.016
    g21: Circle CenterX=-80.4884 CenterY=-16.1925 CenterZ=0 NormalX=0 NormalY=0 NormalZ=1 AngleXU=0 Radius=1.016
    g22: Circle CenterX=-80.4884 CenterY=15.1257 CenterZ=0 NormalX=0 NormalY=0 NormalZ=1 AngleXU=0 Radius=1.016
    g23: Circle CenterX=-5.58377 CenterY=15.1257 CenterZ=0 NormalX=0 NormalY=0 NormalZ=1 AngleXU=0 Radius=1.016
    g24: Circle CenterX=5.76157 CenterY=15.1257 CenterZ=0 NormalX=0 NormalY=0 NormalZ=1 AngleXU=0 Radius=1.016
    g25: Circle CenterX=80.6662 CenterY=15.1257 CenterZ=0 NormalX=0 NormalY=0 NormalZ=1 AngleXU=0 Radius=1.016
  constraints (63):
    c: DistanceX(g0,g0) = 1.651
    c: DistanceY(g0,g0) = 3.9624
    c: Coincident(g0,g-13)
    c: DistanceX(g1,g1) = 1.651
    c: DistanceY(g1,g1) = 3.9624
    c: Coincident(g1,g-13)
    c: DistanceX(g2,g2) = 1.651
    c: DistanceY(g2,g2) = 2.8956
    c: Coincident(g2,g-12)
    c: DistanceX(g3,g3) = 1.651
    c: DistanceY(g3,g3) = 2.8956
    c: Coincident(g3,g-11)
    c: DistanceX(g4,g4) = 1.651
    c: DistanceY(g4,g4) = 2.8956
    c: Coincident(g4,g-9)
    c: DistanceX(g5,g5) = 1.651
    c: DistanceY(g5,g5) = 2.8956
    c: Coincident(g5,g-7)
    c: DistanceX(g6,g6) = 1.651
    c: DistanceY(g6,g6) = 3.9624
    c: Coincident(g6,g-8)
    c: DistanceX(g7,g7) = 1.651
    c: DistanceY(g7,g7) = 3.9624
    c: Coincident(g7,g-9)
    c: Coincident(g8,g3)
    c: PointOnObject(g8,g-2)
    c: Horizontal(g8)
    c: Coincident(g9,g10)
    c: Coincident(g10,g11)
    c: Coincident(g11,g12)
    c: Coincident(g12,g9)
    c: Horizontal(g9)
    c: Horizontal(g11)
    c: Vertical(g10)
    c: Vertical(g12)
    c: Symmetric(g11,g9,g13)
    c: Distance(g9,g11) = 4.445
    c: Coincident(g13,g8)
    c: Diameter(g14) = 5.08
    c: Coincident(g14,g0)
    c: Diameter(g15) = 5.08
    c: Coincident(g15,g1)
    c: Diameter(g16) = 5.08
    c: Coincident(g16,g7)
    c: Diameter(g17) = 5.08
    c: Coincident(g17,g6)
    c: Diameter(g18) = 2.032
    c: Coincident(g18,g0)
    c: Diameter(g19) = 2.032
    c: Coincident(g19,g1)
    c: Diameter(g20) = 2.032
    c: Coincident(g20,g7)
    c: Diameter(g21) = 2.032
    c: Coincident(g21,g6)
    c: Diameter(g22) = 2.032
    c: Coincident(g22,g5)
    c: Diameter(g23) = 2.032
    c: Coincident(g23,g4)
    c: Diameter(g24) = 2.032
    c: Coincident(g24,g3)
    c: Diameter(g25) = 2.032
    c: Coincident(g25,g2)
    c: DistanceX(g11,g11) = 168.656
FEATURE [PartDesign::Pad] Pad001
  BaseFeature = -> Pad
  Direction = (0,0,-1)
  Length = 2.921
  Length2 = 10
  Profile = -> Sketch001
  ReferenceAxis = -> Sketch001 [N_Axis]
  Suppressed = false
  Type = 0
FEATURE [Sketcher::SketchObject] Sketch002
  ArcFitTolerance = 1e-06
  AttachmentSupport = -> [Pad001]
  ExternalGeometry = -> [Pad001]
  FullyConstrained = true
  MakeInternals = false
  MapMode = 5
  Placement = pos=(0,0,0) rot=(1,0,0;3.14159rad)
  sketch-geometry (15):
    g0: LineSegment [constr] StartX=-88.9 StartY=-25.4 StartZ=0 EndX=88.9 EndY=-25.4 EndZ=0
    g1: LineSegment [constr] StartX=88.9 StartY=-25.4 StartZ=0 EndX=88.9 EndY=25.4 EndZ=0
    g2: LineSegment [constr] StartX=88.9 StartY=25.4 StartZ=0 EndX=-88.9 EndY=25.4 EndZ=0
    g3: LineSegment [constr] StartX=-88.9 StartY=25.4 StartZ=0 EndX=-88.9 EndY=-25.4 EndZ=0
    g4: GeomPoint [constr] X=0 Y=0 Z=0
    g5: LineSegment [constr] StartX=84.328 StartY=17.3482 StartZ=0 EndX=84.328 EndY=25.4 EndZ=0
    g6: LineSegment [constr] StartX=-84.328 StartY=17.3482 StartZ=0 EndX=-84.328 EndY=25.4 EndZ=0
    g7: LineSegment StartX=84.328 StartY=25.4 StartZ=0 EndX=84.328 EndY=-25.4 EndZ=0
    g8: LineSegment StartX=84.328 StartY=-25.4 StartZ=0 EndX=88.9 EndY=-25.4 EndZ=0
    g9: LineSegment StartX=88.9 StartY=-25.4 StartZ=0 EndX=88.9 EndY=25.4 EndZ=0
    g10: LineSegment StartX=88.9 StartY=25.4 StartZ=0 EndX=84.328 EndY=25.4 EndZ=0
    g11: LineSegment StartX=-84.328 StartY=25.4 StartZ=0 EndX=-88.9 EndY=25.4 EndZ=0
    g12: LineSegment StartX=-88.9 StartY=25.4 StartZ=0 EndX=-88.9 EndY=-25.4 EndZ=0
    g13: LineSegment StartX=-88.9 StartY=-25.4 StartZ=0 EndX=-84.328 EndY=-25.4 EndZ=0
    g14: LineSegment StartX=-84.328 StartY=-25.4 StartZ=0 EndX=-84.328 EndY=25.4 EndZ=0
  constraints (39):
    c: Coincident(g0,g1)
    c: Coincident(g1,g2)
    c: Coincident(g2,g3)
    c: Coincident(g3,g0)
    c: Horizontal(g0)
    c: Horizontal(g2)
    c: Vertical(g1)
    c: Vertical(g3)
    c: Symmetric(g2,g0,g4)
    c: Distance(g1,g3) = 177.8
    c: Distance(g0,g2) = 50.8
    c: Coincident(g4,g-1)
    c: Coincident(g5,g-8)
    c: PointOnObject(g5,g2)
    c: Vertical(g5)
    c: Perpendicular(g2,g5)
    c: Coincident(g6,g-8)
    c: PointOnObject(g6,g2)
    c: Perpendicular(g2,g6)
    c: Coincident(g7,g8)
    c: Coincident(g8,g9)
    c: Coincident(g9,g10)
    c: Coincident(g10,g7)
    c: Vertical(g7)
    c: Vertical(g9)
    c: Horizontal(g8)
    c: Horizontal(g10)
    c: Coincident(g7,g5)
    c: Coincident(g8,g0)
    c: Coincident(g11,g12)
    c: Coincident(g12,g13)
    c: Coincident(g13,g14)
    c: Coincident(g14,g11)
    c: Horizontal(g11)
    c: Horizontal(g13)
    c: Vertical(g12)
    c: Vertical(g14)
    c: Coincident(g11,g6)
    c: Coincident(g12,g0)
FEATURE [PartDesign::Pad] Pad002
  BaseFeature = -> Pad001
  Direction = (0,0,-1)
  Length = 25.4
  Length2 = 10
  Profile = -> Sketch002
  ReferenceAxis = -> Sketch002 [N_Axis]
  Suppressed = false
  Type = 0
FEATURE [Sketcher::SketchObject] Sketch003
  ArcFitTolerance = 1e-06
  AttachmentSupport = -> [Pad002]
  ExternalGeometry = -> [Pad002]
  FullyConstrained = true
  MakeInternals = false
  MapMode = 5
  Placement = pos=(-88.9,0,0) rot=(0.57735,-0.57735,-0.57735;2.0944rad)
  sketch-geometry (4):
    g0: LineSegment [constr] StartX=-25.4 StartY=-25.4 StartZ=0 EndX=-12.7 EndY=-19.05 EndZ=0
    g1: LineSegment [constr] StartX=25.4 StartY=-25.4 StartZ=0 EndX=15.5677 EndY=-19.05 EndZ=0
    g2: Circle CenterX=-12.7 CenterY=-19.05 CenterZ=0 NormalX=0 NormalY=0 NormalZ=1 AngleXU=0 Radius=1.143
    g3: Circle CenterX=15.5677 CenterY=-19.05 CenterZ=0 NormalX=0 NormalY=0 NormalZ=1 AngleXU=0 Radius=1.143
  constraints (10):
    c: DistanceX(g0,g0) = 12.7
    c: DistanceY(g0,g0) = 6.35
    c: Coincident(g0,g-5)
    c: DistanceX(g1,g1) = 9.83234
    c: DistanceY(g1,g1) = 6.35
    c: Coincident(g1,g-6)
    c: Diameter(g2) = 2.286
    c: Coincident(g2,g0)
    c: Diameter(g3) = 2.286
    c: Coincident(g3,g1)
FEATURE [PartDesign::Hole] Hole
  BaseFeature = -> Pad002
  CustomThreadClearance = 0
  Depth = 177.8
  DepthType = 0
  Diameter = 2.77813
  DrillForDepth = false
  DrillPoint = 1
  DrillPointAngle = 118
  HoleCutCountersinkAngle = 90
  HoleCutCustomValues = false
  HoleCutDepth = 0
  HoleCutDiameter = 0
  HoleCutType = 0
  ModelThread = false
  Profile = -> Sketch003
  Suppressed = false
  Tapered = false
  TaperedAngle = 90
  ThreadClass = 0
  ThreadDepth = 177.8
  ThreadDepthType = 0
  ThreadDirection = 0
  ThreadFit = 0
  ThreadSize = 0
  ThreadType = 0
  Threaded = false
  UseCustomThreadClearance = false
FEATURE [Sketcher::SketchObject] Sketch004
  ArcFitTolerance = 1e-06
  AttachmentSupport = -> [Hole]
  ExternalGeometry = -> [Hole]
  FullyConstrained = true
  MakeInternals = false
  MapMode = 5
  Placement = pos=(0,0,4.0132) rot=(0,0,1;0rad)
  sketch-geometry (6):
    g0: LineSegment [constr] StartX=79.0152 StartY=12.2301 StartZ=0 EndX=79.0152 EndY=20.4026 EndZ=0
    g1: LineSegment [constr] StartX=79.0152 StartY=20.4026 StartZ=0 EndX=79.0152 EndY=28.575 EndZ=0
    g2: LineSegment [constr] StartX=7.41257 StartY=12.2301 StartZ=0 EndX=7.41257 EndY=28.575 EndZ=0
    g3: LineSegment [constr] StartX=79.0152 StartY=20.4026 StartZ=0 EndX=43.2139 EndY=20.4026 EndZ=0
    g4: Circle CenterX=43.2139 CenterY=20.4026 CenterZ=0 NormalX=0 NormalY=0 NormalZ=1 AngleXU=0 Radius=5.08
    g5: LineSegment [constr] StartX=43.2139 StartY=20.4026 StartZ=0 EndX=7.41257 EndY=20.4026 EndZ=0
  constraints (16):
    c: Coincident(g0,g-5)
    c: Vertical(g0)
    c: Coincident(g1,g0)
    c: PointOnObject(g1,g-6)
    c: Vertical(g1)
    c: Equal(g1,g0)
    c: Coincident(g2,g-5)
    c: PointOnObject(g2,g-6)
    c: Vertical(g2)
    c: Coincident(g3,g0)
    c: Horizontal(g3)
    c: Diameter(g4) = 10.16
    c: Coincident(g4,g3)
    c: Coincident(g5,g3)
    c: Symmetric(g2,g2,g5)
    c: Equal(g5,g3)
FEATURE [PartDesign::Hole] Hole001
  BaseFeature = -> Hole
  CustomThreadClearance = 0
  Depth = 2.286
  DepthType = 0
  Diameter = 9.779
  DrillForDepth = false
  DrillPoint = 0
  DrillPointAngle = 121
  HoleCutCountersinkAngle = 90
  HoleCutCustomValues = false
  HoleCutDepth = 0
  HoleCutDiameter = 10.2616
  HoleCutType = 0
  ModelThread = false
  Profile = -> Sketch004
  Suppressed = false
  Tapered = false
  TaperedAngle = 90
  ThreadClass = 0
  ThreadDepth = 2.286
  ThreadDepthType = 0
  ThreadDirection = 0
  ThreadFit = 0
  ThreadSize = 0
  ThreadType = 0
  Threaded = false
  UseCustomThreadClearance = false
FEATURE [Sketcher::SketchObject] Sketch005
  ArcFitTolerance = 1e-06
  AttachmentSupport = -> [Hole001]
  ExternalGeometry = -> [Hole001]
  FullyConstrained = true
  MakeInternals = false
  MapMode = 5
  Placement = pos=(0,0,1.7272) rot=(0,0,1;0rad)
  sketch-geometry (5):
    g0: LineSegment StartX=39.6579 StartY=17.0466 StartZ=0 EndX=46.7699 EndY=17.0466 EndZ=0
    g1: LineSegment StartX=46.7699 StartY=17.0466 StartZ=0 EndX=46.7699 EndY=23.7585 EndZ=0
    g2: LineSegment StartX=46.7699 StartY=23.7585 StartZ=0 EndX=39.6579 EndY=23.7585 EndZ=0
    g3: LineSegment StartX=39.6579 StartY=23.7585 StartZ=0 EndX=39.6579 EndY=17.0466 EndZ=0
    g4: GeomPoint [constr] X=43.2139 Y=20.4026 Z=0
  constraints (12):
    c: Coincident(g0,g1)
    c: Coincident(g1,g2)
    c: Coincident(g2,g3)
    c: Coincident(g3,g0)
    c: Horizontal(g0)
    c: Horizontal(g2)
    c: Vertical(g1)
    c: Vertical(g3)
    c: Symmetric(g2,g0,g4)
    c: Distance(g1,g3) = 7.112
    c: Coincident(g4,g-3)
    c: PointOnObject(g1,g-3)
FEATURE [PartDesign::Pocket] Pocket
  BaseFeature = -> Hole001
  Direction = (0,0,-1)
  Length = 5
  Length2 = 5
  Profile = -> Sketch005
  ReferenceAxis = -> Sketch005 [N_Axis]
  Suppressed = false
  Type = 1
FEATURE [PartDesign::Body] Body
  AllowCompound = false
  Group = -> [Sketch,Pad,Sketch001,Pad001,Sketch002,Pad002,Sketch003,Hole,Sketch004,Hole001,Sketch005,Pocket]
  Origin = -> Origin
  Tip = -> Pocket
---- part obd_wire_top.FCStd = doc fcstd_c4d097d10f7b ----
FCSTD DOCUMENT  (FreeCAD 1.0R39285 (Git))
Label: obd_wire_top
License: All rights reserved
LicenseURL: http://en.wikipedia.org/wiki/All_rights_reserved
objects: Sketcher::SketchObject×4, PartDesign::Pocket×3, Measure::MeasureLength×3, PartDesign::Plane×2, PartDesign::Pad×1, PartDesign::Body×1, App::DocumentObjectGroup×1
note: 23 computed .brp shape members not serialized (recipe doc carries the construction recipe); baked Part::Feature solids carry a one-line shape summary decoded from their .brp

FEATURE [Sketcher::SketchObject] Sketch
  ArcFitTolerance = 1e-06
  AttachmentSupport = -> [XY_Plane]
  FullyConstrained = false
  MakeInternals = false
  MapMode = 5
  sketch-geometry (8):
    g0: LineSegment StartX=1.18376 StartY=6.61182 StartZ=0 EndX=1.18376 EndY=2.80182 EndZ=0
    g1: LineSegment StartX=1.18376 StartY=2.80182 StartZ=0 EndX=15.7888 EndY=2.80182 EndZ=0
    g2: LineSegment StartX=15.7888 StartY=2.80182 StartZ=0 EndX=15.7888 EndY=6.61182 EndZ=0
    g3: LineSegment StartX=15.7888 StartY=6.61182 StartZ=0 EndX=1.18376 EndY=6.61182 EndZ=0
    g4: LineSegment [constr] StartX=1.18376 StartY=4.70682 StartZ=0 EndX=3.08876 EndY=4.70682 EndZ=0
    g5: LineSegment [constr] StartX=15.7888 StartY=4.70682 StartZ=0 EndX=13.8838 EndY=4.70682 EndZ=0
    g6: Circle CenterX=3.08876 CenterY=4.70682 CenterZ=0 NormalX=0 NormalY=0 NormalZ=1 AngleXU=0 Radius=1.27
    g7: Circle CenterX=13.8838 CenterY=4.70682 CenterZ=0 NormalX=0 NormalY=0 NormalZ=1 AngleXU=0 Radius=1.27
  constraints (20):
    c: Coincident(g0,g1)
    c: Coincident(g1,g2)
    c: Coincident(g2,g3)
    c: Coincident(g3,g0)
    c: Vertical(g0)
    c: Vertical(g2)
    c: Horizontal(g1)
    c: Horizontal(g3)
    c: Distance(g0,g2) = 14.605
    c: Distance(g1,g3) = 3.81
    c: Distance(g4) = 1.905
    c: Symmetric(g0,g0,g4)
    c: Horizontal(g4)
    c: Distance(g5) = 1.905
    c: Symmetric(g2,g2,g5)
    c: Horizontal(g5)
    c: Diameter(g6) = 2.54
    c: Coincident(g6,g4)
    c: Coincident(g7,g5)
    c: Equal(g7,g6)
FEATURE [PartDesign::Pad] Pad
  Direction = (0,0,1)
  Length = 6.35
  Length2 = 10
  Profile = -> Sketch
  ReferenceAxis = -> Sketch [N_Axis]
  Refine = true
  Suppressed = false
  Type = 0
FEATURE [PartDesign::Plane] DatumPlane
  AttachmentSupport = -> [Pad]
  Length = 60
  MapMode = 5
  Placement = pos=(0,2.80182,0) rot=(1,0,0;1.5708rad)
  ResizeMode = 0
  Width = 60
FEATURE [Sketcher::SketchObject] Sketch001
  ArcFitTolerance = 1e-06
  AttachmentSupport = -> [Pad]
  ExternalGeometry = -> [Pad]
  FullyConstrained = true
  MakeInternals = false
  MapMode = 5
  Placement = pos=(0,2.80182,0) rot=(1,0,0;1.5708rad)
  sketch-geometry (1):
    g0: Circle CenterX=8.48626 CenterY=6.35 CenterZ=0 NormalX=0 NormalY=0 NormalZ=1 AngleXU=0 Radius=3.4925
  constraints (2):
    c: Diameter(g0) = 6.985
    c: Symmetric(g-3,g-3,g0)
FEATURE [PartDesign::Pocket] Pocket
  BaseFeature = -> Pad
  Direction = (0,1,-2e-16)
  Length = 5
  Length2 = 5
  Profile = -> Sketch001
  ReferenceAxis = -> Sketch001 [N_Axis]
  Refine = true
  Suppressed = false
  Type = 1
FEATURE [PartDesign::Plane] DatumPlane001
  AttachmentSupport = -> [Pocket]
  Length = 60
  MapMode = 5
  Placement = pos=(0,2.80182,0) rot=(1,0,0;1.5708rad)
  ResizeMode = 0
  Width = 60
FEATURE [Sketcher::SketchObject] Sketch003
  ArcFitTolerance = 1e-06
  AttachmentSupport = -> [XZ_Plane]
  ExternalGeometry = -> [Pocket]
  FullyConstrained = false
  MakeInternals = false
  MapMode = 5
  Placement = pos=(0,0,0) rot=(1,0,0;1.5708rad)
  sketch-geometry (5):
    g0: LineSegment StartX=15.7888 StartY=6.35 StartZ=0 EndX=15.7888 EndY=6.35 EndZ=0
    g1: LineSegment StartX=15.7888 StartY=6.35 StartZ=0 EndX=15.7888 EndY=5.715 EndZ=0
    g2: LineSegment StartX=15.7888 StartY=5.715 StartZ=0 EndX=10.3798 EndY=5.715 EndZ=0
    g3: LineSegment StartX=10.3798 StartY=5.715 StartZ=0 EndX=10.489 EndY=7.4666 EndZ=0
    g4: LineSegment StartX=10.489 StartY=7.4666 StartZ=0 EndX=15.7888 EndY=6.35 EndZ=0
  constraints (10):
    c: Coincident(g0,g-3)
    c: Coincident(g0,g-3)
    c: Distance(g1) = 0.635
    c: Coincident(g1,g0)
    c: Vertical(g1)
    c: Coincident(g2,g1)
    c: Horizontal(g2)
    c: Coincident(g3,g2)
    c: Coincident(g4,g3)
    c: Coincident(g4,g0)
FEATURE [PartDesign::Pocket] Pocket001
  BaseFeature = -> Pocket
  Direction = (0,1,-2e-16)
  Length = 5
  Length2 = 5
  Profile = -> Sketch003
  ReferenceAxis = -> Sketch003 [N_Axis]
  Refine = true
  Suppressed = false
  Type = 1
FEATURE [Sketcher::SketchObject] Sketch004
  ArcFitTolerance = 1e-06
  AttachmentSupport = -> [DatumPlane001]
  ExternalGeometry = -> [Pocket001]
  FullyConstrained = false
  MakeInternals = false
  MapMode = 5
  Placement = pos=(0,2.80182,0) rot=(1,0,0;1.5708rad)
  sketch-geometry (8):
    g0: ArcOfCircle CenterX=8.48626 CenterY=6.35 CenterZ=0 NormalX=0 NormalY=0 NormalZ=1 AngleXU=0 Radius=4.0005 StartAngle=3.23698 EndAngle=6.0264
    g1: LineSegment [constr] StartX=15.7888 StartY=5.715 StartZ=0 EndX=15.7888 EndY=5.334 EndZ=0
    g2: LineSegment [constr] StartX=1.18376 StartY=6.35 StartZ=0 EndX=1.18376 EndY=5.969 EndZ=0
    g3: LineSegment StartX=1.18376 StartY=5.969 StartZ=0 EndX=4.50394 EndY=5.969 EndZ=0
    g4: LineSegment StartX=15.7888 StartY=5.334 StartZ=0 EndX=12.3556 EndY=5.334 EndZ=0
    g5: LineSegment StartX=15.7888 StartY=5.334 StartZ=0 EndX=18.4948 EndY=-0.939653 EndZ=0
    g6: LineSegment StartX=18.4948 StartY=-0.939653 StartZ=0 EndX=0.279079 EndY=-0.939653 EndZ=0
    g7: LineSegment StartX=0.279079 StartY=-0.939653 StartZ=0 EndX=1.18376 EndY=5.969 EndZ=0
  constraints (19):
    c: Diameter(g0) = 8.001
    c: Coincident(g0,g-3)
    c: Distance(g1) = 0.381
    c: Coincident(g1,g-7)
    c: PointOnObject(g1,g-7)
    c: Distance(g2) = 0.381
    c: Coincident(g2,g-6)
    c: PointOnObject(g2,g-6)
    c: Coincident(g3,g2)
    c: Horizontal(g3)
    c: Coincident(g4,g1)
    c: Horizontal(g4)
    c: Coincident(g5,g1)
    c: Coincident(g6,g5)
    c: Horizontal(g6)
    c: Coincident(g7,g6)
    c: Coincident(g7,g2)
    c: Coincident(g0,g4)
    c: Coincident(g0,g3)
FEATURE [PartDesign::Pocket] Pocket002
  BaseFeature = -> Pocket001
  Direction = (0,1,-2e-16)
  Length = 5
  Length2 = 5
  Profile = -> Sketch004
  ReferenceAxis = -> Sketch004 [N_Axis]
  Refine = true
  Suppressed = false
  Type = 1
FEATURE [PartDesign::Body] Body
  AllowCompound = false
  Group = -> [Sketch,Pad,DatumPlane,Sketch001,Pocket,DatumPlane001,Sketch003,Pocket001,Sketch004,Pocket002]
  Origin = -> Origin
  Tip = -> Pocket002
FEATURE [Measure::MeasureLength] Length  label="Length: 0.5750 ""
  Elements = -> [Body]
  Length = 14.605
FEATURE [Measure::MeasureLength] Length001  label="Length001: 0.1500 ""
  Elements = -> [Body]
  Length = 3.81
FEATURE [Measure::MeasureLength] Length002  label="Length002: 0.2500 ""
  Elements = -> [Body]
  Length = 6.35
FEATURE [App::DocumentObjectGroup] Measurements
  Group = -> [Length,Length001,Length002]
---- part side_left.FCStd = doc fcstd_3f89cc1a9bb9 ----
FCSTD DOCUMENT  (FreeCAD 1.0R39285 (Git))
Label: side_left
License: All rights reserved
LicenseURL: http://en.wikipedia.org/wiki/All_rights_reserved
objects: Sketcher::SketchObject×4, PartDesign::Fillet×3, PartDesign::Pad×2, PartDesign::Pocket×1, PartDesign::Hole×1, PartDesign::Body×1, Part::FeaturePython×1
note: 31 computed .brp shape members not serialized (recipe doc carries the construction recipe); baked Part::Feature solids carry a one-line shape summary decoded from their .brp

FEATURE [Sketcher::SketchObject] Sketch
  ArcFitTolerance = 1e-06
  AttachmentSupport = -> [XY_Plane]
  FullyConstrained = true
  MakeInternals = false
  MapMode = 5
  sketch-geometry (5):
    g0: LineSegment StartX=-63.5 StartY=-25.4 StartZ=0 EndX=63.5 EndY=-25.4 EndZ=0
    g1: LineSegment StartX=63.5 StartY=-25.4 StartZ=0 EndX=63.5 EndY=25.4 EndZ=0
    g2: LineSegment StartX=63.5 StartY=25.4 StartZ=0 EndX=-63.5 EndY=25.4 EndZ=0
    g3: LineSegment StartX=-63.5 StartY=25.4 StartZ=0 EndX=-63.5 EndY=-25.4 EndZ=0
    g4: GeomPoint [constr] X=0 Y=0 Z=0
  constraints (12):
    c: Coincident(g0,g1)
    c: Coincident(g1,g2)
    c: Coincident(g2,g3)
    c: Coincident(g3,g0)
    c: Horizontal(g0)
    c: Horizontal(g2)
    c: Vertical(g1)
    c: Vertical(g3)
    c: Symmetric(g2,g0,g4)
    c: Distance(g1,g3) = 127
    c: Distance(g0,g2) = 50.8
    c: Coincident(g4,g-1)
FEATURE [PartDesign::Pad] Pad
  Direction = (0,0,1)
  Length = 5.08
  Length2 = 10
  Profile = -> Sketch
  ReferenceAxis = -> Sketch [N_Axis]
  Suppressed = false
  Type = 0
FEATURE [Sketcher::SketchObject] Sketch001
  ArcFitTolerance = 1e-06
  AttachmentSupport = -> [Pad]
  ExternalGeometry = -> [Pad]
  FullyConstrained = false
  MakeInternals = false
  MapMode = 5
  Placement = pos=(0,0,5.08) rot=(0,0,1;0rad)
  sketch-geometry (19):
    g0: LineSegment [constr] StartX=63.5 StartY=-25.4 StartZ=0 EndX=57.15 EndY=-25.4 EndZ=0
    g1: LineSegment [constr] StartX=57.15 StartY=-25.4 StartZ=0 EndX=57.15 EndY=-15.5673 EndZ=0
    g2: LineSegment [constr] StartX=57.15 StartY=-15.5673 StartZ=0 EndX=57.15 EndY=12.7 EndZ=0
    g3: LineSegment [constr] StartX=57.15 StartY=12.7 StartZ=0 EndX=57.15 EndY=25.4 EndZ=0
    g4: Circle CenterX=57.15 CenterY=12.7 CenterZ=0 NormalX=0 NormalY=0 NormalZ=1 AngleXU=0 Radius=1.5875
    g5: Circle CenterX=57.15 CenterY=-15.5673 CenterZ=0 NormalX=0 NormalY=0 NormalZ=1 AngleXU=0 Radius=1.5875
    g6: LineSegment [constr] StartX=57.15 StartY=-25.4 StartZ=0 EndX=51.5983 EndY=-25.4 EndZ=0
    g7: LineSegment [constr] StartX=51.5983 StartY=-25.4 StartZ=0 EndX=47.5851 EndY=-21.1328 EndZ=0
    g8: LineSegment [constr] StartX=-63.5 StartY=-25.4 StartZ=0 EndX=-59.4868 EndY=-21.3868 EndZ=0
    g9: LineSegment [constr] StartX=-63.5 StartY=25.4 StartZ=0 EndX=-59.4868 EndY=21.3868 EndZ=0
    g10: LineSegment [constr] StartX=47.5851 StartY=-21.1328 StartZ=0 EndX=47.5851 EndY=19.226 EndZ=0
    g11: LineSegment [constr] StartX=47.5851 StartY=25.4 StartZ=0 EndX=47.5851 EndY=21.3868 EndZ=0
    g12: LineSegment StartX=-54.0779 StartY=-21.3868 StartZ=0 EndX=47.5851 EndY=-21.3868 EndZ=0
    g13: LineSegment StartX=47.5851 StartY=-21.3868 StartZ=0 EndX=47.5851 EndY=19.226 EndZ=0
    g14: LineSegment StartX=42.1761 StartY=21.3868 StartZ=0 EndX=-59.4868 EndY=21.3868 EndZ=0
    g15: LineSegment StartX=-59.4868 StartY=21.3868 StartZ=0 EndX=-59.4868 EndY=-19.226 EndZ=0
    g16: LineSegment StartX=-59.4868 StartY=-19.226 StartZ=0 EndX=42.1761 EndY=21.3868 EndZ=0
    g17: LineSegment StartX=-54.0779 StartY=-21.3868 StartZ=0 EndX=47.5851 EndY=19.226 EndZ=0
    g18: LineSegment [constr] StartX=47.5851 StartY=21.3868 StartZ=0 EndX=47.5851 EndY=25.4 EndZ=0
  constraints (47):
    c: Distance(g0) = 6.35
    c: Coincident(g0,g-5)
    c: PointOnObject(g0,g-5)
    c: Coincident(g1,g0)
    c: Vertical(g1)
    c: Block(g1)
    c: Coincident(g2,g1)
    c: Vertical(g2)
    c: Coincident(g3,g2)
    c: PointOnObject(g3,g-3)
    c: Vertical(g3)
    c: DistanceY(g3,g3) = 12.7
    c: Diameter(g4) = 3.175
    c: Coincident(g4,g2)
    c: Diameter(g5) = 3.175
    c: Coincident(g5,g1)
    c: Coincident(g6,g0)
    c: Horizontal(g6)
    c: Block(g6)
    c: DistanceX(g7,g7) = 4.0132
    c: DistanceY(g7,g7) = 4.2672
    c: Coincident(g7,g6)
    c: DistanceX(g8,g8) = 4.0132
    c: DistanceY(g8,g8) = 4.0132
    c: Coincident(g8,g-5)
    c: DistanceX(g9,g9) = 4.0132
    c: DistanceY(g9,g9) = 4.0132
    c: Coincident(g9,g-3)
    c: Coincident(g10,g7)
    c: PointOnObject(g18,g-3)
    c: Vertical(g10)
    c: DistanceX(g11,g11) = 0
    c: DistanceY(g11,g11) = 4.0132
    c: Coincident(g11,g18)
    c: Coincident(g12,g13)
    c: Coincident(g14,g15)
    c: Horizontal(g12)
    c: Horizontal(g14)
    c: Vertical(g13)
    c: Vertical(g15)
    c: PointOnObject(g17,g10)
    c: PointOnObject(g13,g17)
    c: Coincident(g12,g17)
    c: Coincident(g15,g16)
    c: Coincident(g14,g16)
    c: PointOnObject(g10,g13)
    c: PointOnObject(g18,g11)
FEATURE [PartDesign::Pocket] Pocket
  BaseFeature = -> Pad
  Direction = (0,0,-1)
  Length = 5
  Length2 = 5
  Profile = -> Sketch001
  ReferenceAxis = -> Sketch001 [N_Axis]
  Suppressed = false
  Type = 1
FEATURE [PartDesign::Fillet] Fillet
  Base = -> Pocket [Edge33,Edge29]
  BaseFeature = -> Pocket
  Radius = 0.999998
  SupportTransform = false
  Suppressed = false
  UseAllEdges = false
FEATURE [PartDesign::Fillet] Fillet001
  Base = -> Fillet [Edge17,Edge37]
  BaseFeature = -> Fillet
  Radius = 0.999998
  SupportTransform = false
  Suppressed = false
  UseAllEdges = false
FEATURE [PartDesign::Fillet] Fillet002
  Base = -> Fillet001 [Edge25,Edge47]
  BaseFeature = -> Fillet001
  Radius = 0.999998
  SupportTransform = false
  Suppressed = false
  UseAllEdges = false
FEATURE [Sketcher::SketchObject] Sketch002
  ArcFitTolerance = 1e-06
  AttachmentSupport = -> [Fillet002]
  ExternalGeometry = -> [Fillet002]
  FullyConstrained = true
  MakeInternals = false
  MapMode = 5
  Placement = pos=(0,0,5.08) rot=(0,0,1;0rad)
  sketch-geometry (9):
    g0: LineSegment StartX=-63.5 StartY=-25.4 StartZ=0 EndX=-53.34 EndY=-25.4 EndZ=0
    g1: LineSegment StartX=-53.34 StartY=-25.4 StartZ=0 EndX=-53.34 EndY=-21.3868 EndZ=0
    g2: LineSegment StartX=-53.34 StartY=-21.3868 StartZ=0 EndX=-63.5 EndY=-21.3868 EndZ=0
    g3: LineSegment StartX=-63.5 StartY=-21.3868 StartZ=0 EndX=-63.5 EndY=-25.4 EndZ=0
    g4: LineSegment [constr] StartX=-63.5 StartY=-25.4 StartZ=0 EndX=38.1 EndY=-25.4 EndZ=0
    g5: LineSegment StartX=38.1 StartY=-25.4 StartZ=0 EndX=38.1 EndY=-21.3868 EndZ=0
    g6: LineSegment StartX=38.1 StartY=-21.3868 StartZ=0 EndX=27.94 EndY=-21.3868 EndZ=0
    g7: LineSegment StartX=27.94 StartY=-21.3868 StartZ=0 EndX=27.94 EndY=-25.4 EndZ=0
    g8: LineSegment StartX=27.94 StartY=-25.4 StartZ=0 EndX=38.1 EndY=-25.4 EndZ=0
  constraints (25):
    c: Coincident(g0,g1)
    c: Coincident(g1,g2)
    c: Coincident(g2,g3)
    c: Coincident(g3,g0)
    c: Horizontal(g0)
    c: Horizontal(g2)
    c: Vertical(g1)
    c: Vertical(g3)
    c: Distance(g1,g3) = 10.16
    c: Distance(g0,g2) = 4.0132
    c: Coincident(g0,g-4)
    c: Distance(g4) = 101.6
    c: Coincident(g4,g0)
    c: PointOnObject(g4,g-4)
    c: Coincident(g5,g6)
    c: Coincident(g6,g7)
    c: Coincident(g7,g8)
    c: Coincident(g8,g5)
    c: Vertical(g5)
    c: Vertical(g7)
    c: Horizontal(g6)
    c: Horizontal(g8)
    c: Distance(g5,g7) = 10.16
    c: Distance(g6,g8) = 4.0132
    c: Coincident(g5,g4)
FEATURE [PartDesign::Pad] Pad001
  BaseFeature = -> Fillet002
  Direction = (0,0,1)
  Length = 10.16
  Length2 = 10
  Profile = -> Sketch002
  ReferenceAxis = -> Sketch002 [N_Axis]
  Suppressed = false
  Type = 0
FEATURE [Sketcher::SketchObject] Sketch003
  ArcFitTolerance = 1e-06
  AttachmentSupport = -> [Pad001]
  ExternalGeometry = -> [Pad001]
  FullyConstrained = true
  MakeInternals = false
  MapMode = 5
  Placement = pos=(0,-25.4,0) rot=(1,0,0;1.5708rad)
  sketch-geometry (10):
    g0: LineSegment [constr] StartX=27.94 StartY=15.24 StartZ=0 EndX=27.94 EndY=10.16 EndZ=0
    g1: LineSegment [constr] StartX=27.94 StartY=10.16 StartZ=0 EndX=27.94 EndY=5.08 EndZ=0
    g2: LineSegment [constr] StartX=27.94 StartY=10.16 StartZ=0 EndX=33.02 EndY=10.16 EndZ=0
    g3: LineSegment [constr] StartX=33.02 StartY=10.16 StartZ=0 EndX=38.1 EndY=10.16 EndZ=0
    g4: LineSegment [constr] StartX=-63.5 StartY=5.08 StartZ=0 EndX=-63.5 EndY=10.16 EndZ=0
    g5: LineSegment [constr] StartX=-63.5 StartY=10.16 StartZ=0 EndX=-63.5 EndY=15.24 EndZ=0
    g6: LineSegment [constr] StartX=-63.5 StartY=10.16 StartZ=0 EndX=-58.42 EndY=10.16 EndZ=0
    g7: LineSegment [constr] StartX=-58.42 StartY=10.16 StartZ=0 EndX=-53.34 EndY=10.16 EndZ=0
    g8: Circle CenterX=-58.42 CenterY=10.16 CenterZ=0 NormalX=0 NormalY=0 NormalZ=1 AngleXU=0 Radius=1.143
    g9: Circle CenterX=33.02 CenterY=10.16 CenterZ=0 NormalX=0 NormalY=0 NormalZ=1 AngleXU=0 Radius=1.143
  constraints (24):
    c: Coincident(g0,g-8)
    c: Symmetric(g-7,g-7,g0)
    c: Coincident(g1,g0)
    c: Coincident(g1,g-10)
    c: Coincident(g2,g0)
    c: Horizontal(g2)
    c: Coincident(g3,g2)
    c: Symmetric(g-9,g-9,g3)
    c: Coincident(g4,g-5)
    c: PointOnObject(g4,g-4)
    c: Coincident(g5,g4)
    c: Coincident(g5,g-4)
    c: Coincident(g6,g4)
    c: Horizontal(g6)
    c: Coincident(g7,g6)
    c: PointOnObject(g7,g-6)
    c: Horizontal(g7)
    c: Equal(g4,g5)
    c: Equal(g6,g7)
    c: Equal(g2,g3)
    c: Diameter(g8) = 2.286
    c: Coincident(g8,g6)
    c: Diameter(g9) = 2.286
    c: Coincident(g9,g2)
FEATURE [PartDesign::Hole] Hole
  BaseFeature = -> Pad001
  CustomThreadClearance = 0
  Depth = 278.012
  DepthType = 1
  Diameter = 2.77813
  DrillForDepth = false
  DrillPoint = 1
  DrillPointAngle = 118
  HoleCutCountersinkAngle = 90
  HoleCutCustomValues = false
  HoleCutDepth = 0
  HoleCutDiameter = 0
  HoleCutType = 0
  ModelThread = false
  Profile = -> Sketch003
  Suppressed = false
  Tapered = false
  TaperedAngle = 90
  ThreadClass = 0
  ThreadDepth = 278.012
  ThreadDepthType = 0
  ThreadDirection = 0
  ThreadFit = 0
  ThreadSize = 0
  ThreadType = 0
  Threaded = false
  UseCustomThreadClearance = false
FEATURE [PartDesign::Body] Body
  AllowCompound = false
  Group = -> [Sketch,Pad,Sketch001,Pocket,Fillet,Fillet001,Fillet002,Sketch002,Pad001,Sketch003,Hole]
  Origin = -> Origin
  Tip = -> Hole
FEATURE [Part::FeaturePython] Clone  label="Hole001"  # Draft clone (typed FeaturePython)
  AttacherType = Attacher::AttachEngine3D
  Fuse = false
  Objects = -> [Hole]
  Placement = pos=(0,0,-41.9999) rot=(0,0,1;0rad)
  Scale = (1,1,-1)
---- part side_right.FCStd = doc fcstd_784035cf4b67 ----
FCSTD DOCUMENT  (FreeCAD 1.0R39285 (Git))
Label: side_right
License: All rights reserved
LicenseURL: http://en.wikipedia.org/wiki/All_rights_reserved
objects: Sketcher::SketchObject×4, PartDesign::Fillet×3, PartDesign::Pad×2, PartDesign::Pocket×1, PartDesign::Hole×1, PartDesign::Body×1
note: 30 computed .brp shape members not serialized (recipe doc carries the construction recipe); baked Part::Feature solids carry a one-line shape summary decoded from their .brp

FEATURE [Sketcher::SketchObject] Sketch
  ArcFitTolerance = 1e-06
  AttachmentSupport = -> [XY_Plane]
  FullyConstrained = true
  MakeInternals = false
  MapMode = 5
  sketch-geometry (5):
    g0: LineSegment StartX=-63.5 StartY=-25.4 StartZ=0 EndX=63.5 EndY=-25.4 EndZ=0
    g1: LineSegment StartX=63.5 StartY=-25.4 StartZ=0 EndX=63.5 EndY=25.4 EndZ=0
    g2: LineSegment StartX=63.5 StartY=25.4 StartZ=0 EndX=-63.5 EndY=25.4 EndZ=0
    g3: LineSegment StartX=-63.5 StartY=25.4 StartZ=0 EndX=-63.5 EndY=-25.4 EndZ=0
    g4: GeomPoint [constr] X=0 Y=0 Z=0
  constraints (12):
    c: Coincident(g0,g1)
    c: Coincident(g1,g2)
    c: Coincident(g2,g3)
    c: Coincident(g3,g0)
    c: Horizontal(g0)
    c: Horizontal(g2)
    c: Vertical(g1)
    c: Vertical(g3)
    c: Symmetric(g2,g0,g4)
    c: Distance(g1,g3) = 127
    c: Distance(g0,g2) = 50.8
    c: Coincident(g4,g-1)
FEATURE [PartDesign::Pad] Pad
  Direction = (0,0,1)
  Length = 5.08
  Length2 = 10
  Profile = -> Sketch
  ReferenceAxis = -> Sketch [N_Axis]
  Suppressed = false
  Type = 0
FEATURE [Sketcher::SketchObject] Sketch001
  ArcFitTolerance = 1e-06
  AttachmentSupport = -> [Pad]
  ExternalGeometry = -> [Pad]
  FullyConstrained = false
  MakeInternals = false
  MapMode = 5
  Placement = pos=(0,0,5.08) rot=(0,0,1;0rad)
  sketch-geometry (19):
    g0: LineSegment [constr] StartX=63.5 StartY=-25.4 StartZ=0 EndX=57.15 EndY=-25.4 EndZ=0
    g1: LineSegment [constr] StartX=57.15 StartY=-25.4 StartZ=0 EndX=57.15 EndY=-15.5673 EndZ=0
    g2: LineSegment [constr] StartX=57.15 StartY=-15.5673 StartZ=0 EndX=57.15 EndY=12.7 EndZ=0
    g3: LineSegment [constr] StartX=57.15 StartY=12.7 StartZ=0 EndX=57.15 EndY=25.4 EndZ=0
    g4: Circle CenterX=57.15 CenterY=12.7 CenterZ=0 NormalX=0 NormalY=0 NormalZ=1 AngleXU=0 Radius=1.5875
    g5: Circle CenterX=57.15 CenterY=-15.5673 CenterZ=0 NormalX=0 NormalY=0 NormalZ=1 AngleXU=0 Radius=1.5875
    g6: LineSegment [constr] StartX=57.15 StartY=-25.4 StartZ=0 EndX=51.5983 EndY=-25.4 EndZ=0
    g7: LineSegment [constr] StartX=51.5983 StartY=-25.4 StartZ=0 EndX=47.5851 EndY=-21.1328 EndZ=0
    g8: LineSegment [constr] StartX=-63.5 StartY=-25.4 StartZ=0 EndX=-59.4868 EndY=-21.3868 EndZ=0
    g9: LineSegment [constr] StartX=-63.5 StartY=25.4 StartZ=0 EndX=-59.4868 EndY=21.3868 EndZ=0
    g10: LineSegment [constr] StartX=47.5851 StartY=-21.1328 StartZ=0 EndX=47.5851 EndY=19.226 EndZ=0
    g11: LineSegment [constr] StartX=47.5851 StartY=25.4 StartZ=0 EndX=47.5851 EndY=21.3868 EndZ=0
    g12: LineSegment StartX=-54.0779 StartY=-21.3868 StartZ=0 EndX=47.5851 EndY=-21.3868 EndZ=0
    g13: LineSegment StartX=47.5851 StartY=-21.3868 StartZ=0 EndX=47.5851 EndY=19.226 EndZ=0
    g14: LineSegment StartX=42.1761 StartY=21.3868 StartZ=0 EndX=-59.4868 EndY=21.3868 EndZ=0
    g15: LineSegment StartX=-59.4868 StartY=21.3868 StartZ=0 EndX=-59.4868 EndY=-19.226 EndZ=0
    g16: LineSegment StartX=-59.4868 StartY=-19.226 StartZ=0 EndX=42.1761 EndY=21.3868 EndZ=0
    g17: LineSegment StartX=-54.0779 StartY=-21.3868 StartZ=0 EndX=47.5851 EndY=19.226 EndZ=0
    g18: LineSegment [constr] StartX=47.5851 StartY=21.3868 StartZ=0 EndX=47.5851 EndY=25.4 EndZ=0
  constraints (47):
    c: Distance(g0) = 6.35
    c: Coincident(g0,g-5)
    c: PointOnObject(g0,g-5)
    c: Coincident(g1,g0)
    c: Vertical(g1)
    c: Block(g1)
    c: Coincident(g2,g1)
    c: Vertical(g2)
    c: Coincident(g3,g2)
    c: PointOnObject(g3,g-3)
    c: Vertical(g3)
    c: DistanceY(g3,g3) = 12.7
    c: Diameter(g4) = 3.175
    c: Coincident(g4,g2)
    c: Diameter(g5) = 3.175
    c: Coincident(g5,g1)
    c: Coincident(g6,g0)
    c: Horizontal(g6)
    c: Block(g6)
    c: DistanceX(g7,g7) = 4.0132
    c: DistanceY(g7,g7) = 4.2672
    c: Coincident(g7,g6)
    c: DistanceX(g8,g8) = 4.0132
    c: DistanceY(g8,g8) = 4.0132
    c: Coincident(g8,g-5)
    c: DistanceX(g9,g9) = 4.0132
    c: DistanceY(g9,g9) = 4.0132
    c: Coincident(g9,g-3)
    c: Coincident(g10,g7)
    c: PointOnObject(g18,g-3)
    c: Vertical(g10)
    c: DistanceX(g11,g11) = 0
    c: DistanceY(g11,g11) = 4.0132
    c: Coincident(g11,g18)
    c: Coincident(g12,g13)
    c: Coincident(g14,g15)
    c: Horizontal(g12)
    c: Horizontal(g14)
    c: Vertical(g13)
    c: Vertical(g15)
    c: PointOnObject(g17,g10)
    c: PointOnObject(g13,g17)
    c: Coincident(g12,g17)
    c: Coincident(g15,g16)
    c: Coincident(g14,g16)
    c: PointOnObject(g10,g13)
    c: PointOnObject(g18,g11)
FEATURE [PartDesign::Pocket] Pocket
  BaseFeature = -> Pad
  Direction = (0,0,-1)
  Length = 5
  Length2 = 5
  Profile = -> Sketch001
  ReferenceAxis = -> Sketch001 [N_Axis]
  Suppressed = false
  Type = 1
FEATURE [PartDesign::Fillet] Fillet
  Base = -> Pocket [Edge33,Edge29]
  BaseFeature = -> Pocket
  Radius = 0.999998
  SupportTransform = false
  Suppressed = false
  UseAllEdges = false
FEATURE [PartDesign::Fillet] Fillet001
  Base = -> Fillet [Edge17,Edge37]
  BaseFeature = -> Fillet
  Radius = 0.999998
  SupportTransform = false
  Suppressed = false
  UseAllEdges = false
FEATURE [PartDesign::Fillet] Fillet002
  Base = -> Fillet001 [Edge25,Edge47]
  BaseFeature = -> Fillet001
  Radius = 0.999998
  SupportTransform = false
  Suppressed = false
  UseAllEdges = false
FEATURE [Sketcher::SketchObject] Sketch002
  ArcFitTolerance = 1e-06
  AttachmentSupport = -> [Fillet002]
  ExternalGeometry = -> [Fillet002]
  FullyConstrained = true
  MakeInternals = false
  MapMode = 5
  Placement = pos=(0,0,5.08) rot=(0,0,1;0rad)
  sketch-geometry (9):
    g0: LineSegment StartX=-63.5 StartY=-25.4 StartZ=0 EndX=-53.34 EndY=-25.4 EndZ=0
    g1: LineSegment StartX=-53.34 StartY=-25.4 StartZ=0 EndX=-53.34 EndY=-21.3868 EndZ=0
    g2: LineSegment StartX=-53.34 StartY=-21.3868 StartZ=0 EndX=-63.5 EndY=-21.3868 EndZ=0
    g3: LineSegment StartX=-63.5 StartY=-21.3868 StartZ=0 EndX=-63.5 EndY=-25.4 EndZ=0
    g4: LineSegment [constr] StartX=-63.5 StartY=-25.4 StartZ=0 EndX=38.1 EndY=-25.4 EndZ=0
    g5: LineSegment StartX=38.1 StartY=-25.4 StartZ=0 EndX=38.1 EndY=-21.3868 EndZ=0
    g6: LineSegment StartX=38.1 StartY=-21.3868 StartZ=0 EndX=27.94 EndY=-21.3868 EndZ=0
    g7: LineSegment StartX=27.94 StartY=-21.3868 StartZ=0 EndX=27.94 EndY=-25.4 EndZ=0
    g8: LineSegment StartX=27.94 StartY=-25.4 StartZ=0 EndX=38.1 EndY=-25.4 EndZ=0
  constraints (25):
    c: Coincident(g0,g1)
    c: Coincident(g1,g2)
    c: Coincident(g2,g3)
    c: Coincident(g3,g0)
    c: Horizontal(g0)
    c: Horizontal(g2)
    c: Vertical(g1)
    c: Vertical(g3)
    c: Distance(g1,g3) = 10.16
    c: Distance(g0,g2) = 4.0132
    c: Coincident(g0,g-4)
    c: Distance(g4) = 101.6
    c: Coincident(g4,g0)
    c: PointOnObject(g4,g-4)
    c: Coincident(g5,g6)
    c: Coincident(g6,g7)
    c: Coincident(g7,g8)
    c: Coincident(g8,g5)
    c: Vertical(g5)
    c: Vertical(g7)
    c: Horizontal(g6)
    c: Horizontal(g8)
    c: Distance(g5,g7) = 10.16
    c: Distance(g6,g8) = 4.0132
    c: Coincident(g5,g4)
FEATURE [PartDesign::Pad] Pad001
  BaseFeature = -> Fillet002
  Direction = (0,0,1)
  Length = 10.16
  Length2 = 10
  Profile = -> Sketch002
  ReferenceAxis = -> Sketch002 [N_Axis]
  Suppressed = false
  Type = 0
FEATURE [Sketcher::SketchObject] Sketch003
  ArcFitTolerance = 1e-06
  AttachmentSupport = -> [Pad001]
  ExternalGeometry = -> [Pad001]
  FullyConstrained = true
  MakeInternals = false
  MapMode = 5
  Placement = pos=(0,-25.4,0) rot=(1,0,0;1.5708rad)
  sketch-geometry (10):
    g0: LineSegment [constr] StartX=27.94 StartY=15.24 StartZ=0 EndX=27.94 EndY=10.16 EndZ=0
    g1: LineSegment [constr] StartX=27.94 StartY=10.16 StartZ=0 EndX=27.94 EndY=5.08 EndZ=0
    g2: LineSegment [constr] StartX=27.94 StartY=10.16 StartZ=0 EndX=33.02 EndY=10.16 EndZ=0
    g3: LineSegment [constr] StartX=33.02 StartY=10.16 StartZ=0 EndX=38.1 EndY=10.16 EndZ=0
    g4: LineSegment [constr] StartX=-63.5 StartY=5.08 StartZ=0 EndX=-63.5 EndY=10.16 EndZ=0
    g5: LineSegment [constr] StartX=-63.5 StartY=10.16 StartZ=0 EndX=-63.5 EndY=15.24 EndZ=0
    g6: LineSegment [constr] StartX=-63.5 StartY=10.16 StartZ=0 EndX=-58.42 EndY=10.16 EndZ=0
    g7: LineSegment [constr] StartX=-58.42 StartY=10.16 StartZ=0 EndX=-53.34 EndY=10.16 EndZ=0
    g8: Circle CenterX=-58.42 CenterY=10.16 CenterZ=0 NormalX=0 NormalY=0 NormalZ=1 AngleXU=0 Radius=1.143
    g9: Circle CenterX=33.02 CenterY=10.16 CenterZ=0 NormalX=0 NormalY=0 NormalZ=1 AngleXU=0 Radius=1.143
  constraints (24):
    c: Coincident(g0,g-8)
    c: Symmetric(g-7,g-7,g0)
    c: Coincident(g1,g0)
    c: Coincident(g1,g-10)
    c: Coincident(g2,g0)
    c: Horizontal(g2)
    c: Coincident(g3,g2)
    c: Symmetric(g-9,g-9,g3)
    c: Coincident(g4,g-5)
    c: PointOnObject(g4,g-4)
    c: Coincident(g5,g4)
    c: Coincident(g5,g-4)
    c: Coincident(g6,g4)
    c: Horizontal(g6)
    c: Coincident(g7,g6)
    c: PointOnObject(g7,g-6)
    c: Horizontal(g7)
    c: Equal(g4,g5)
    c: Equal(g6,g7)
    c: Equal(g2,g3)
    c: Diameter(g8) = 2.286
    c: Coincident(g8,g6)
    c: Diameter(g9) = 2.286
    c: Coincident(g9,g2)
FEATURE [PartDesign::Hole] Hole
  BaseFeature = -> Pad001
  CustomThreadClearance = 0
  Depth = 278.012
  DepthType = 1
  Diameter = 2.77813
  DrillForDepth = false
  DrillPoint = 1
  DrillPointAngle = 118
  HoleCutCountersinkAngle = 90
  HoleCutCustomValues = false
  HoleCutDepth = 0
  HoleCutDiameter = 0
  HoleCutType = 0
  ModelThread = false
  Profile = -> Sketch003
  Suppressed = false
  Tapered = false
  TaperedAngle = 90
  ThreadClass = 0
  ThreadDepth = 278.012
  ThreadDepthType = 0
  ThreadDirection = 0
  ThreadFit = 0
  ThreadSize = 0
  ThreadType = 0
  Threaded = false
  UseCustomThreadClearance = false
FEATURE [PartDesign::Body] Body
  AllowCompound = false
  Group = -> [Sketch,Pad,Sketch001,Pocket,Fillet,Fillet001,Fillet002,Sketch002,Pad001,Sketch003,Hole]
  Origin = -> Origin
  Tip = -> Hole
